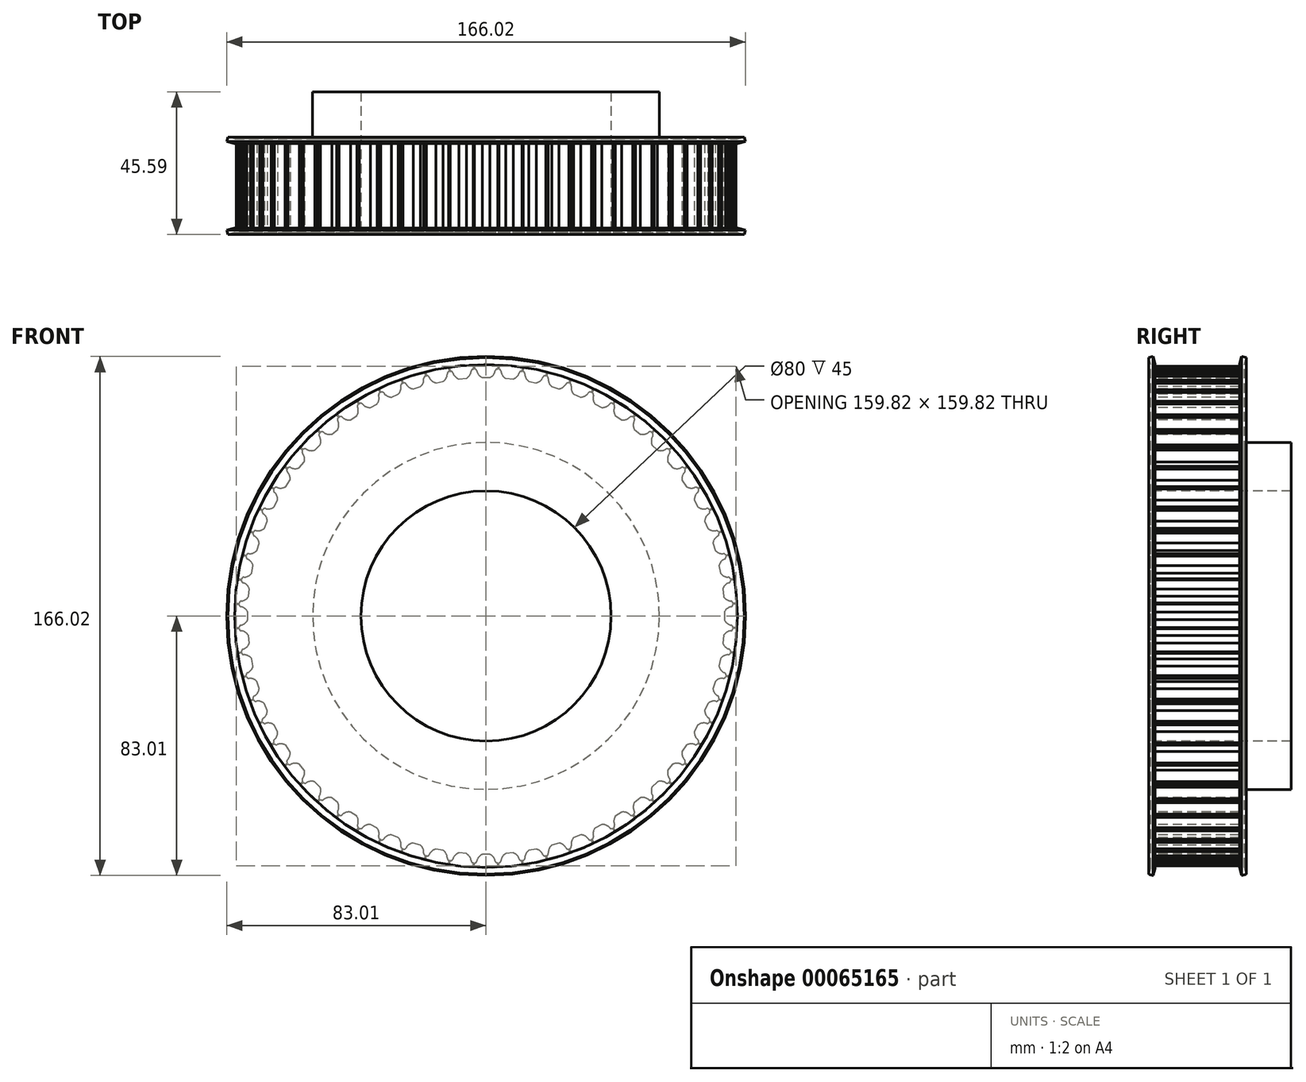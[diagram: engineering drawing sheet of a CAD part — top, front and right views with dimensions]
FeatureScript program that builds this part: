
annotation { "Feature Type Name" : "Feature", "Feature Type Description" : "" }
export const myFeature = defineFeature(function(context is Context, id is Id, definition is map)
    precondition{}
    {
        {
            var Q0;
            Q0=qCreatedBy(makeId("Right.planeOp"),FACE);
            var sketch = newSketch(context, id + "F0", { "sketchPlane" : qUnion([Q0])});
            skLineSegment(sketch, "E0", {"start": v(-21.52, 0) * mm, "end": v(23.89, 0) * mm, "construction": true});
            skLineSegment(sketch, "E1", {"start": v(0, 40) * mm, "end": v(0, 80) * mm});
            skLineSegment(sketch, "E2", {"start": v(0, 80) * mm, "end": v(30, 80) * mm});
            skLineSegment(sketch, "E3", {"start": v(30, 80) * mm, "end": v(30, 55.5) * mm});
            skLineSegment(sketch, "E4", {"start": v(30, 55.5) * mm, "end": v(45, 55.5) * mm});
            skLineSegment(sketch, "E5", {"start": v(45, 55.5) * mm, "end": v(45, 40) * mm});
            skLineSegment(sketch, "E6", {"start": v(45, 40) * mm, "end": v(0, 40) * mm});
            skSolve(sketch);
        }
        {
            var Q0;
            Q0=qSketchRegion(id+"F0",true);
            var Q1;
            Q1=sQuery(id+"F0.wireOp",EDGE,"E0");
            revolve(context, id + "F1", {"entities" : qUnion([Q0]), "axis" : qUnion([Q1]), "revolveType" : RevolveType.FULL});
        }
        {
            var Q0;
            Q0=qCreatedBy(makeId("Right.planeOp"),FACE);
            var sketch = newSketch(context, id + "F2", { "sketchPlane" : qUnion([Q0])});
            skLineSegment(sketch, "E7", {"start": v(-38.96, 0) * mm, "end": v(60.95, 0) * mm, "construction": true});
            skSolve(sketch);
        }
        {
            var Q0;
            Q0=makeQuery(id+"F1.opRevolve","SWEPT_FACE",FACE,{"disambiguationData":[OSD([sQuery(id+"F0.wireOp",EDGE,"E1")])]});
            var sketch = newSketch(context, id + "F3", { "sketchPlane" : qUnion([Q0])});
            skLineSegment(sketch, "E8.bottom", {"start": v(-3.75, 81) * mm, "end": v(3.75, 81) * mm});
            skLineSegment(sketch, "E8.top", {"start": v(3.67, 79) * mm, "end": v(3.75, 79) * mm});
            skLineSegment(sketch, "E8.left", {"start": v(-3.75, 81) * mm, "end": v(-3.75, 79) * mm});
            skLineSegment(sketch, "E8.right", {"start": v(3.75, 81) * mm, "end": v(3.75, 79) * mm});
            skArc(sketch, "E9", {"start": v(-2.94, 78.4) * mm, "mid": v(-2.33, 77.11) * mm, "end": v(-1.2, 76.25) * mm});
            skLineSegment(sketch, "E10", {"start": v(-1.2, 76.25) * mm, "end": v(1.2, 76.25) * mm});
            skArc(sketch, "E11.trimOffspring", {"start": v(1.2, 76.25) * mm, "mid": v(2.33, 77.11) * mm, "end": v(2.94, 78.4) * mm});
            skArc(sketch, "E12.filletArc", {"start": v(3.67, 79) * mm, "mid": v(3.2, 78.83) * mm, "end": v(2.94, 78.4) * mm});
            skLineSegment(sketch, "E13", {"start": v(-3.75, 79) * mm, "end": v(-3.67, 79) * mm});
            skPoint(sketch, "E14.visualSharp", {"position": v(-3, 79) * mm});
            skArc(sketch, "E14.filletArc", {"start": v(-2.94, 78.4) * mm, "mid": v(-3.2, 78.83) * mm, "end": v(-3.67, 79) * mm});
            skLineSegment(sketch, "E15.1.0", {"start": v(-11.67, 80.24) * mm, "end": v(-4.2, 80.98) * mm});
            skLineSegment(sketch, "E15.1.1", {"start": v(-11.67, 80.24) * mm, "end": v(-11.48, 78.25) * mm});
            skLineSegment(sketch, "E15.1.2", {"start": v(-11.48, 78.25) * mm, "end": v(-11.4, 78.26) * mm});
            skArc(sketch, "E15.1.3", {"start": v(-10.6, 77.73) * mm, "mid": v(-10.91, 78.14) * mm, "end": v(-11.4, 78.26) * mm});
            skArc(sketch, "E15.1.4", {"start": v(-10.6, 77.73) * mm, "mid": v(-9.88, 76.51) * mm, "end": v(-8.67, 75.77) * mm});
            skLineSegment(sketch, "E15.1.5", {"start": v(-8.67, 75.77) * mm, "end": v(-6.28, 76) * mm});
            skArc(sketch, "E15.1.6", {"start": v(-6.28, 76) * mm, "mid": v(-5.24, 76.97) * mm, "end": v(-4.76, 78.31) * mm});
            skArc(sketch, "E15.1.7", {"start": v(-4.09, 78.98) * mm, "mid": v(-4.54, 78.76) * mm, "end": v(-4.76, 78.31) * mm});
            skLineSegment(sketch, "E15.1.8", {"start": v(-4.09, 78.98) * mm, "end": v(-4.01, 78.99) * mm});
            skLineSegment(sketch, "E15.1.9", {"start": v(-4.2, 80.98) * mm, "end": v(-4.01, 78.99) * mm});
            skLineSegment(sketch, "E15.2.0", {"start": v(-19.48, 78.71) * mm, "end": v(-12.12, 80.18) * mm});
            skLineSegment(sketch, "E15.2.1", {"start": v(-19.48, 78.71) * mm, "end": v(-19.1, 76.75) * mm});
            skLineSegment(sketch, "E15.2.2", {"start": v(-19.1, 76.75) * mm, "end": v(-19.02, 76.77) * mm});
            skArc(sketch, "E15.2.3", {"start": v(-18.18, 76.32) * mm, "mid": v(-18.52, 76.7) * mm, "end": v(-19.02, 76.77) * mm});
            skArc(sketch, "E15.2.4", {"start": v(-18.18, 76.32) * mm, "mid": v(-17.33, 75.18) * mm, "end": v(-16.05, 74.55) * mm});
            skLineSegment(sketch, "E15.2.5", {"start": v(-16.05, 74.55) * mm, "end": v(-13.7, 75.02) * mm});
            skArc(sketch, "E15.2.6", {"start": v(-13.7, 75.02) * mm, "mid": v(-12.76, 76.09) * mm, "end": v(-12.41, 77.47) * mm});
            skArc(sketch, "E15.2.7", {"start": v(-11.8, 78.2) * mm, "mid": v(-12.24, 77.94) * mm, "end": v(-12.41, 77.47) * mm});
            skLineSegment(sketch, "E15.2.8", {"start": v(-11.8, 78.2) * mm, "end": v(-11.73, 78.21) * mm});
            skLineSegment(sketch, "E15.2.9", {"start": v(-12.12, 80.18) * mm, "end": v(-11.73, 78.21) * mm});
            skLineSegment(sketch, "E15.3.0", {"start": v(-27.1, 76.42) * mm, "end": v(-19.92, 78.6) * mm});
            skLineSegment(sketch, "E15.3.1", {"start": v(-27.1, 76.42) * mm, "end": v(-26.52, 74.5) * mm});
            skLineSegment(sketch, "E15.3.2", {"start": v(-26.52, 74.5) * mm, "end": v(-26.45, 74.53) * mm});
            skArc(sketch, "E15.3.3", {"start": v(-25.57, 74.17) * mm, "mid": v(-25.95, 74.5) * mm, "end": v(-26.45, 74.53) * mm});
            skArc(sketch, "E15.3.4", {"start": v(-25.57, 74.17) * mm, "mid": v(-24.62, 73.12) * mm, "end": v(-23.28, 72.62) * mm});
            skLineSegment(sketch, "E15.3.5", {"start": v(-23.28, 72.62) * mm, "end": v(-20.99, 73.31) * mm});
            skArc(sketch, "E15.3.6", {"start": v(-20.99, 73.31) * mm, "mid": v(-20.15, 74.47) * mm, "end": v(-19.95, 75.88) * mm});
            skArc(sketch, "E15.3.7", {"start": v(-19.42, 76.66) * mm, "mid": v(-19.82, 76.37) * mm, "end": v(-19.95, 75.88) * mm});
            skLineSegment(sketch, "E15.3.8", {"start": v(-19.42, 76.66) * mm, "end": v(-19.34, 76.69) * mm});
            skLineSegment(sketch, "E15.3.9", {"start": v(-19.92, 78.6) * mm, "end": v(-19.34, 76.69) * mm});
            skLineSegment(sketch, "E15.4.0", {"start": v(-34.46, 73.4) * mm, "end": v(-27.53, 76.27) * mm});
            skLineSegment(sketch, "E15.4.1", {"start": v(-34.46, 73.4) * mm, "end": v(-33.7, 71.55) * mm});
            skLineSegment(sketch, "E15.4.2", {"start": v(-33.7, 71.55) * mm, "end": v(-33.63, 71.58) * mm});
            skArc(sketch, "E15.4.3", {"start": v(-32.72, 71.3) * mm, "mid": v(-33.12, 71.6) * mm, "end": v(-33.63, 71.58) * mm});
            skArc(sketch, "E15.4.4", {"start": v(-32.72, 71.3) * mm, "mid": v(-31.66, 70.35) * mm, "end": v(-30.29, 69.99) * mm});
            skLineSegment(sketch, "E15.4.5", {"start": v(-30.29, 69.99) * mm, "end": v(-28.07, 70.9) * mm});
            skArc(sketch, "E15.4.6", {"start": v(-28.07, 70.9) * mm, "mid": v(-27.36, 72.13) * mm, "end": v(-27.29, 73.56) * mm});
            skArc(sketch, "E15.4.7", {"start": v(-26.84, 74.4) * mm, "mid": v(-27.21, 74.05) * mm, "end": v(-27.29, 73.56) * mm});
            skLineSegment(sketch, "E15.4.8", {"start": v(-26.84, 74.4) * mm, "end": v(-26.77, 74.42) * mm});
            skLineSegment(sketch, "E15.4.9", {"start": v(-27.53, 76.27) * mm, "end": v(-26.77, 74.42) * mm});
            skLineSegment(sketch, "E15.5.0", {"start": v(-41.5, 69.67) * mm, "end": v(-34.88, 73.2) * mm});
            skLineSegment(sketch, "E15.5.1", {"start": v(-41.5, 69.67) * mm, "end": v(-40.55, 67.9) * mm});
            skLineSegment(sketch, "E15.5.2", {"start": v(-40.55, 67.9) * mm, "end": v(-40.48, 67.94) * mm});
            skArc(sketch, "E15.5.3", {"start": v(-39.55, 67.76) * mm, "mid": v(-39.98, 68.01) * mm, "end": v(-40.48, 67.94) * mm});
            skArc(sketch, "E15.5.4", {"start": v(-39.55, 67.76) * mm, "mid": v(-38.4, 66.9) * mm, "end": v(-37, 66.68) * mm});
            skLineSegment(sketch, "E15.5.5", {"start": v(-37, 66.68) * mm, "end": v(-34.89, 67.81) * mm});
            skArc(sketch, "E15.5.6", {"start": v(-34.89, 67.81) * mm, "mid": v(-34.3, 69.1) * mm, "end": v(-34.37, 70.53) * mm});
            skArc(sketch, "E15.5.7", {"start": v(-34, 71.4) * mm, "mid": v(-34.34, 71.03) * mm, "end": v(-34.37, 70.53) * mm});
            skLineSegment(sketch, "E15.5.8", {"start": v(-34, 71.4) * mm, "end": v(-33.93, 71.44) * mm});
            skLineSegment(sketch, "E15.5.9", {"start": v(-34.88, 73.2) * mm, "end": v(-33.93, 71.44) * mm});
            skLineSegment(sketch, "E15.6.0", {"start": v(-48.12, 65.27) * mm, "end": v(-41.88, 69.43) * mm});
            skLineSegment(sketch, "E15.6.1", {"start": v(-48.12, 65.27) * mm, "end": v(-47, 63.6) * mm});
            skLineSegment(sketch, "E15.6.2", {"start": v(-47, 63.6) * mm, "end": v(-46.95, 63.64) * mm});
            skArc(sketch, "E15.6.3", {"start": v(-46, 63.55) * mm, "mid": v(-46.46, 63.77) * mm, "end": v(-46.95, 63.64) * mm});
            skArc(sketch, "E15.6.4", {"start": v(-46, 63.55) * mm, "mid": v(-44.78, 62.82) * mm, "end": v(-43.36, 62.73) * mm});
            skLineSegment(sketch, "E15.6.5", {"start": v(-43.36, 62.73) * mm, "end": v(-41.37, 64.07) * mm});
            skArc(sketch, "E15.6.6", {"start": v(-41.37, 64.07) * mm, "mid": v(-40.9, 65.41) * mm, "end": v(-41.11, 66.82) * mm});
            skArc(sketch, "E15.6.7", {"start": v(-40.84, 67.73) * mm, "mid": v(-41.14, 67.32) * mm, "end": v(-41.11, 66.82) * mm});
            skLineSegment(sketch, "E15.6.8", {"start": v(-40.84, 67.73) * mm, "end": v(-40.77, 67.77) * mm});
            skLineSegment(sketch, "E15.6.9", {"start": v(-41.88, 69.43) * mm, "end": v(-40.77, 67.77) * mm});
            skLineSegment(sketch, "E15.7.0", {"start": v(-54.28, 60.23) * mm, "end": v(-48.49, 65) * mm});
            skLineSegment(sketch, "E15.7.1", {"start": v(-54.28, 60.23) * mm, "end": v(-53.02, 58.69) * mm});
            skLineSegment(sketch, "E15.7.2", {"start": v(-53.02, 58.69) * mm, "end": v(-52.96, 58.74) * mm});
            skArc(sketch, "E15.7.3", {"start": v(-52, 58.74) * mm, "mid": v(-52.48, 58.9) * mm, "end": v(-52.96, 58.74) * mm});
            skArc(sketch, "E15.7.4", {"start": v(-52, 58.74) * mm, "mid": v(-50.72, 58.13) * mm, "end": v(-49.3, 58.18) * mm});
            skLineSegment(sketch, "E15.7.5", {"start": v(-49.3, 58.18) * mm, "end": v(-47.45, 59.7) * mm});
            skArc(sketch, "E15.7.6", {"start": v(-47.45, 59.7) * mm, "mid": v(-47.12, 61.09) * mm, "end": v(-47.46, 62.47) * mm});
            skArc(sketch, "E15.7.7", {"start": v(-47.28, 63.4) * mm, "mid": v(-47.54, 62.97) * mm, "end": v(-47.46, 62.47) * mm});
            skLineSegment(sketch, "E15.7.8", {"start": v(-47.28, 63.4) * mm, "end": v(-47.22, 63.45) * mm});
            skLineSegment(sketch, "E15.7.9", {"start": v(-48.49, 65) * mm, "end": v(-47.22, 63.45) * mm});
            skLineSegment(sketch, "E15.8.0", {"start": v(-59.93, 54.62) * mm, "end": v(-54.62, 59.93) * mm});
            skLineSegment(sketch, "E15.8.1", {"start": v(-59.93, 54.62) * mm, "end": v(-58.51, 53.2) * mm});
            skLineSegment(sketch, "E15.8.2", {"start": v(-58.51, 53.2) * mm, "end": v(-58.46, 53.26) * mm});
            skArc(sketch, "E15.8.3", {"start": v(-57.52, 53.36) * mm, "mid": v(-58, 53.48) * mm, "end": v(-58.46, 53.26) * mm});
            skArc(sketch, "E15.8.4", {"start": v(-57.52, 53.36) * mm, "mid": v(-56.18, 52.88) * mm, "end": v(-54.76, 53.07) * mm});
            skLineSegment(sketch, "E15.8.5", {"start": v(-54.76, 53.07) * mm, "end": v(-53.07, 54.76) * mm});
            skArc(sketch, "E15.8.6", {"start": v(-53.07, 54.76) * mm, "mid": v(-52.88, 56.18) * mm, "end": v(-53.36, 57.52) * mm});
            skArc(sketch, "E15.8.7", {"start": v(-53.26, 58.46) * mm, "mid": v(-53.48, 58) * mm, "end": v(-53.36, 57.52) * mm});
            skLineSegment(sketch, "E15.8.8", {"start": v(-53.26, 58.46) * mm, "end": v(-53.2, 58.51) * mm});
            skLineSegment(sketch, "E15.8.9", {"start": v(-54.62, 59.93) * mm, "end": v(-53.2, 58.51) * mm});
            skLineSegment(sketch, "E15.9.0", {"start": v(-65, 48.49) * mm, "end": v(-60.23, 54.28) * mm});
            skLineSegment(sketch, "E15.9.1", {"start": v(-65, 48.49) * mm, "end": v(-63.45, 47.22) * mm});
            skLineSegment(sketch, "E15.9.2", {"start": v(-63.45, 47.22) * mm, "end": v(-63.4, 47.28) * mm});
            skArc(sketch, "E15.9.3", {"start": v(-62.47, 47.46) * mm, "mid": v(-62.97, 47.54) * mm, "end": v(-63.4, 47.28) * mm});
            skArc(sketch, "E15.9.4", {"start": v(-62.47, 47.46) * mm, "mid": v(-61.09, 47.12) * mm, "end": v(-59.7, 47.45) * mm});
            skLineSegment(sketch, "E15.9.5", {"start": v(-59.7, 47.45) * mm, "end": v(-58.18, 49.3) * mm});
            skArc(sketch, "E15.9.6", {"start": v(-58.18, 49.3) * mm, "mid": v(-58.13, 50.72) * mm, "end": v(-58.74, 52) * mm});
            skArc(sketch, "E15.9.7", {"start": v(-58.74, 52.96) * mm, "mid": v(-58.9, 52.48) * mm, "end": v(-58.74, 52) * mm});
            skLineSegment(sketch, "E15.9.8", {"start": v(-58.74, 52.96) * mm, "end": v(-58.69, 53.02) * mm});
            skLineSegment(sketch, "E15.9.9", {"start": v(-60.23, 54.28) * mm, "end": v(-58.69, 53.02) * mm});
            skLineSegment(sketch, "E15.10.0", {"start": v(-69.43, 41.88) * mm, "end": v(-65.27, 48.12) * mm});
            skLineSegment(sketch, "E15.10.1", {"start": v(-69.43, 41.88) * mm, "end": v(-67.77, 40.77) * mm});
            skLineSegment(sketch, "E15.10.2", {"start": v(-67.77, 40.77) * mm, "end": v(-67.73, 40.84) * mm});
            skArc(sketch, "E15.10.3", {"start": v(-66.82, 41.11) * mm, "mid": v(-67.32, 41.14) * mm, "end": v(-67.73, 40.84) * mm});
            skArc(sketch, "E15.10.4", {"start": v(-66.82, 41.11) * mm, "mid": v(-65.41, 40.9) * mm, "end": v(-64.07, 41.37) * mm});
            skLineSegment(sketch, "E15.10.5", {"start": v(-64.07, 41.37) * mm, "end": v(-62.73, 43.36) * mm});
            skArc(sketch, "E15.10.6", {"start": v(-62.73, 43.36) * mm, "mid": v(-62.82, 44.78) * mm, "end": v(-63.55, 46) * mm});
            skArc(sketch, "E15.10.7", {"start": v(-63.64, 46.95) * mm, "mid": v(-63.77, 46.46) * mm, "end": v(-63.55, 46) * mm});
            skLineSegment(sketch, "E15.10.8", {"start": v(-63.64, 46.95) * mm, "end": v(-63.6, 47) * mm});
            skLineSegment(sketch, "E15.10.9", {"start": v(-65.27, 48.12) * mm, "end": v(-63.6, 47) * mm});
            skLineSegment(sketch, "E15.11.0", {"start": v(-73.2, 34.88) * mm, "end": v(-69.67, 41.5) * mm});
            skLineSegment(sketch, "E15.11.1", {"start": v(-73.2, 34.88) * mm, "end": v(-71.44, 33.93) * mm});
            skLineSegment(sketch, "E15.11.2", {"start": v(-71.44, 33.93) * mm, "end": v(-71.4, 34) * mm});
            skArc(sketch, "E15.11.3", {"start": v(-70.53, 34.37) * mm, "mid": v(-71.03, 34.34) * mm, "end": v(-71.4, 34) * mm});
            skArc(sketch, "E15.11.4", {"start": v(-70.53, 34.37) * mm, "mid": v(-69.1, 34.3) * mm, "end": v(-67.81, 34.89) * mm});
            skLineSegment(sketch, "E15.11.5", {"start": v(-67.81, 34.89) * mm, "end": v(-66.68, 37) * mm});
            skArc(sketch, "E15.11.6", {"start": v(-66.68, 37) * mm, "mid": v(-66.9, 38.4) * mm, "end": v(-67.76, 39.55) * mm});
            skArc(sketch, "E15.11.7", {"start": v(-67.94, 40.48) * mm, "mid": v(-68.01, 39.98) * mm, "end": v(-67.76, 39.55) * mm});
            skLineSegment(sketch, "E15.11.8", {"start": v(-67.94, 40.48) * mm, "end": v(-67.9, 40.55) * mm});
            skLineSegment(sketch, "E15.11.9", {"start": v(-69.67, 41.5) * mm, "end": v(-67.9, 40.55) * mm});
            skLineSegment(sketch, "E15.12.0", {"start": v(-76.27, 27.53) * mm, "end": v(-73.4, 34.46) * mm});
            skLineSegment(sketch, "E15.12.1", {"start": v(-76.27, 27.53) * mm, "end": v(-74.42, 26.77) * mm});
            skLineSegment(sketch, "E15.12.2", {"start": v(-74.42, 26.77) * mm, "end": v(-74.4, 26.84) * mm});
            skArc(sketch, "E15.12.3", {"start": v(-73.56, 27.29) * mm, "mid": v(-74.05, 27.21) * mm, "end": v(-74.4, 26.84) * mm});
            skArc(sketch, "E15.12.4", {"start": v(-73.56, 27.29) * mm, "mid": v(-72.13, 27.36) * mm, "end": v(-70.9, 28.07) * mm});
            skLineSegment(sketch, "E15.12.5", {"start": v(-70.9, 28.07) * mm, "end": v(-69.99, 30.29) * mm});
            skArc(sketch, "E15.12.6", {"start": v(-69.99, 30.29) * mm, "mid": v(-70.35, 31.66) * mm, "end": v(-71.3, 32.72) * mm});
            skArc(sketch, "E15.12.7", {"start": v(-71.58, 33.63) * mm, "mid": v(-71.6, 33.12) * mm, "end": v(-71.3, 32.72) * mm});
            skLineSegment(sketch, "E15.12.8", {"start": v(-71.58, 33.63) * mm, "end": v(-71.55, 33.7) * mm});
            skLineSegment(sketch, "E15.12.9", {"start": v(-73.4, 34.46) * mm, "end": v(-71.55, 33.7) * mm});
            skLineSegment(sketch, "E15.13.0", {"start": v(-78.6, 19.92) * mm, "end": v(-76.42, 27.1) * mm});
            skLineSegment(sketch, "E15.13.1", {"start": v(-78.6, 19.92) * mm, "end": v(-76.69, 19.34) * mm});
            skLineSegment(sketch, "E15.13.2", {"start": v(-76.69, 19.34) * mm, "end": v(-76.66, 19.42) * mm});
            skArc(sketch, "E15.13.3", {"start": v(-75.88, 19.95) * mm, "mid": v(-76.37, 19.82) * mm, "end": v(-76.66, 19.42) * mm});
            skArc(sketch, "E15.13.4", {"start": v(-75.88, 19.95) * mm, "mid": v(-74.47, 20.15) * mm, "end": v(-73.31, 20.99) * mm});
            skLineSegment(sketch, "E15.13.5", {"start": v(-73.31, 20.99) * mm, "end": v(-72.62, 23.28) * mm});
            skArc(sketch, "E15.13.6", {"start": v(-72.62, 23.28) * mm, "mid": v(-73.12, 24.62) * mm, "end": v(-74.17, 25.57) * mm});
            skArc(sketch, "E15.13.7", {"start": v(-74.53, 26.45) * mm, "mid": v(-74.5, 25.95) * mm, "end": v(-74.17, 25.57) * mm});
            skLineSegment(sketch, "E15.13.8", {"start": v(-74.53, 26.45) * mm, "end": v(-74.5, 26.52) * mm});
            skLineSegment(sketch, "E15.13.9", {"start": v(-76.42, 27.1) * mm, "end": v(-74.5, 26.52) * mm});
            skLineSegment(sketch, "E15.14.0", {"start": v(-80.18, 12.12) * mm, "end": v(-78.71, 19.48) * mm});
            skLineSegment(sketch, "E15.14.1", {"start": v(-80.18, 12.12) * mm, "end": v(-78.21, 11.73) * mm});
            skLineSegment(sketch, "E15.14.2", {"start": v(-78.21, 11.73) * mm, "end": v(-78.2, 11.8) * mm});
            skArc(sketch, "E15.14.3", {"start": v(-77.47, 12.41) * mm, "mid": v(-77.94, 12.24) * mm, "end": v(-78.2, 11.8) * mm});
            skArc(sketch, "E15.14.4", {"start": v(-77.47, 12.41) * mm, "mid": v(-76.09, 12.76) * mm, "end": v(-75.02, 13.7) * mm});
            skLineSegment(sketch, "E15.14.5", {"start": v(-75.02, 13.7) * mm, "end": v(-74.55, 16.05) * mm});
            skArc(sketch, "E15.14.6", {"start": v(-74.55, 16.05) * mm, "mid": v(-75.18, 17.33) * mm, "end": v(-76.32, 18.18) * mm});
            skArc(sketch, "E15.14.7", {"start": v(-76.77, 19.02) * mm, "mid": v(-76.7, 18.52) * mm, "end": v(-76.32, 18.18) * mm});
            skLineSegment(sketch, "E15.14.8", {"start": v(-76.77, 19.02) * mm, "end": v(-76.75, 19.1) * mm});
            skLineSegment(sketch, "E15.14.9", {"start": v(-78.71, 19.48) * mm, "end": v(-76.75, 19.1) * mm});
            skLineSegment(sketch, "E15.15.0", {"start": v(-80.98, 4.2) * mm, "end": v(-80.24, 11.67) * mm});
            skLineSegment(sketch, "E15.15.1", {"start": v(-80.98, 4.2) * mm, "end": v(-78.99, 4.01) * mm});
            skLineSegment(sketch, "E15.15.2", {"start": v(-78.99, 4.01) * mm, "end": v(-78.98, 4.09) * mm});
            skArc(sketch, "E15.15.3", {"start": v(-78.31, 4.76) * mm, "mid": v(-78.76, 4.54) * mm, "end": v(-78.98, 4.09) * mm});
            skArc(sketch, "E15.15.4", {"start": v(-78.31, 4.76) * mm, "mid": v(-76.97, 5.24) * mm, "end": v(-76, 6.28) * mm});
            skLineSegment(sketch, "E15.15.5", {"start": v(-76, 6.28) * mm, "end": v(-75.77, 8.67) * mm});
            skArc(sketch, "E15.15.6", {"start": v(-75.77, 8.67) * mm, "mid": v(-76.51, 9.88) * mm, "end": v(-77.73, 10.6) * mm});
            skArc(sketch, "E15.15.7", {"start": v(-78.26, 11.4) * mm, "mid": v(-78.14, 10.91) * mm, "end": v(-77.73, 10.6) * mm});
            skLineSegment(sketch, "E15.15.8", {"start": v(-78.26, 11.4) * mm, "end": v(-78.25, 11.48) * mm});
            skLineSegment(sketch, "E15.15.9", {"start": v(-80.24, 11.67) * mm, "end": v(-78.25, 11.48) * mm});
            skLineSegment(sketch, "E15.16.0", {"start": v(-81, -3.75) * mm, "end": v(-81, 3.75) * mm});
            skLineSegment(sketch, "E15.16.1", {"start": v(-81, -3.75) * mm, "end": v(-79, -3.75) * mm});
            skLineSegment(sketch, "E15.16.2", {"start": v(-79, -3.75) * mm, "end": v(-79, -3.67) * mm});
            skArc(sketch, "E15.16.3", {"start": v(-78.4, -2.94) * mm, "mid": v(-78.83, -3.2) * mm, "end": v(-79, -3.67) * mm});
            skArc(sketch, "E15.16.4", {"start": v(-78.4, -2.94) * mm, "mid": v(-77.11, -2.33) * mm, "end": v(-76.25, -1.2) * mm});
            skLineSegment(sketch, "E15.16.5", {"start": v(-76.25, -1.2) * mm, "end": v(-76.25, 1.2) * mm});
            skArc(sketch, "E15.16.6", {"start": v(-76.25, 1.2) * mm, "mid": v(-77.11, 2.33) * mm, "end": v(-78.4, 2.94) * mm});
            skArc(sketch, "E15.16.7", {"start": v(-79, 3.67) * mm, "mid": v(-78.83, 3.2) * mm, "end": v(-78.4, 2.94) * mm});
            skLineSegment(sketch, "E15.16.8", {"start": v(-79, 3.67) * mm, "end": v(-79, 3.75) * mm});
            skLineSegment(sketch, "E15.16.9", {"start": v(-81, 3.75) * mm, "end": v(-79, 3.75) * mm});
            skLineSegment(sketch, "E15.17.0", {"start": v(-80.24, -11.67) * mm, "end": v(-80.98, -4.2) * mm});
            skLineSegment(sketch, "E15.17.1", {"start": v(-80.24, -11.67) * mm, "end": v(-78.25, -11.48) * mm});
            skLineSegment(sketch, "E15.17.2", {"start": v(-78.25, -11.48) * mm, "end": v(-78.26, -11.4) * mm});
            skArc(sketch, "E15.17.3", {"start": v(-77.73, -10.6) * mm, "mid": v(-78.14, -10.91) * mm, "end": v(-78.26, -11.4) * mm});
            skArc(sketch, "E15.17.4", {"start": v(-77.73, -10.6) * mm, "mid": v(-76.51, -9.88) * mm, "end": v(-75.77, -8.67) * mm});
            skLineSegment(sketch, "E15.17.5", {"start": v(-75.77, -8.67) * mm, "end": v(-76, -6.28) * mm});
            skArc(sketch, "E15.17.6", {"start": v(-76, -6.28) * mm, "mid": v(-76.97, -5.24) * mm, "end": v(-78.31, -4.76) * mm});
            skArc(sketch, "E15.17.7", {"start": v(-78.98, -4.09) * mm, "mid": v(-78.76, -4.54) * mm, "end": v(-78.31, -4.76) * mm});
            skLineSegment(sketch, "E15.17.8", {"start": v(-78.98, -4.09) * mm, "end": v(-78.99, -4.01) * mm});
            skLineSegment(sketch, "E15.17.9", {"start": v(-80.98, -4.2) * mm, "end": v(-78.99, -4.01) * mm});
            skLineSegment(sketch, "E15.18.0", {"start": v(-78.71, -19.48) * mm, "end": v(-80.18, -12.12) * mm});
            skLineSegment(sketch, "E15.18.1", {"start": v(-78.71, -19.48) * mm, "end": v(-76.75, -19.1) * mm});
            skLineSegment(sketch, "E15.18.2", {"start": v(-76.75, -19.1) * mm, "end": v(-76.77, -19.02) * mm});
            skArc(sketch, "E15.18.3", {"start": v(-76.32, -18.18) * mm, "mid": v(-76.7, -18.52) * mm, "end": v(-76.77, -19.02) * mm});
            skArc(sketch, "E15.18.4", {"start": v(-76.32, -18.18) * mm, "mid": v(-75.18, -17.33) * mm, "end": v(-74.55, -16.05) * mm});
            skLineSegment(sketch, "E15.18.5", {"start": v(-74.55, -16.05) * mm, "end": v(-75.02, -13.7) * mm});
            skArc(sketch, "E15.18.6", {"start": v(-75.02, -13.7) * mm, "mid": v(-76.09, -12.76) * mm, "end": v(-77.47, -12.41) * mm});
            skArc(sketch, "E15.18.7", {"start": v(-78.2, -11.8) * mm, "mid": v(-77.94, -12.24) * mm, "end": v(-77.47, -12.41) * mm});
            skLineSegment(sketch, "E15.18.8", {"start": v(-78.2, -11.8) * mm, "end": v(-78.21, -11.73) * mm});
            skLineSegment(sketch, "E15.18.9", {"start": v(-80.18, -12.12) * mm, "end": v(-78.21, -11.73) * mm});
            skLineSegment(sketch, "E15.19.0", {"start": v(-76.42, -27.1) * mm, "end": v(-78.6, -19.92) * mm});
            skLineSegment(sketch, "E15.19.1", {"start": v(-76.42, -27.1) * mm, "end": v(-74.5, -26.52) * mm});
            skLineSegment(sketch, "E15.19.2", {"start": v(-74.5, -26.52) * mm, "end": v(-74.53, -26.45) * mm});
            skArc(sketch, "E15.19.3", {"start": v(-74.17, -25.57) * mm, "mid": v(-74.5, -25.95) * mm, "end": v(-74.53, -26.45) * mm});
            skArc(sketch, "E15.19.4", {"start": v(-74.17, -25.57) * mm, "mid": v(-73.12, -24.62) * mm, "end": v(-72.62, -23.28) * mm});
            skLineSegment(sketch, "E15.19.5", {"start": v(-72.62, -23.28) * mm, "end": v(-73.31, -20.99) * mm});
            skArc(sketch, "E15.19.6", {"start": v(-73.31, -20.99) * mm, "mid": v(-74.47, -20.15) * mm, "end": v(-75.88, -19.95) * mm});
            skArc(sketch, "E15.19.7", {"start": v(-76.66, -19.42) * mm, "mid": v(-76.37, -19.82) * mm, "end": v(-75.88, -19.95) * mm});
            skLineSegment(sketch, "E15.19.8", {"start": v(-76.66, -19.42) * mm, "end": v(-76.69, -19.34) * mm});
            skLineSegment(sketch, "E15.19.9", {"start": v(-78.6, -19.92) * mm, "end": v(-76.69, -19.34) * mm});
            skLineSegment(sketch, "E15.20.0", {"start": v(-73.4, -34.46) * mm, "end": v(-76.27, -27.53) * mm});
            skLineSegment(sketch, "E15.20.1", {"start": v(-73.4, -34.46) * mm, "end": v(-71.55, -33.7) * mm});
            skLineSegment(sketch, "E15.20.2", {"start": v(-71.55, -33.7) * mm, "end": v(-71.58, -33.63) * mm});
            skArc(sketch, "E15.20.3", {"start": v(-71.3, -32.72) * mm, "mid": v(-71.6, -33.12) * mm, "end": v(-71.58, -33.63) * mm});
            skArc(sketch, "E15.20.4", {"start": v(-71.3, -32.72) * mm, "mid": v(-70.35, -31.66) * mm, "end": v(-69.99, -30.29) * mm});
            skLineSegment(sketch, "E15.20.5", {"start": v(-69.99, -30.29) * mm, "end": v(-70.9, -28.07) * mm});
            skArc(sketch, "E15.20.6", {"start": v(-70.9, -28.07) * mm, "mid": v(-72.13, -27.36) * mm, "end": v(-73.56, -27.29) * mm});
            skArc(sketch, "E15.20.7", {"start": v(-74.4, -26.84) * mm, "mid": v(-74.05, -27.21) * mm, "end": v(-73.56, -27.29) * mm});
            skLineSegment(sketch, "E15.20.8", {"start": v(-74.4, -26.84) * mm, "end": v(-74.42, -26.77) * mm});
            skLineSegment(sketch, "E15.20.9", {"start": v(-76.27, -27.53) * mm, "end": v(-74.42, -26.77) * mm});
            skLineSegment(sketch, "E15.21.0", {"start": v(-69.67, -41.5) * mm, "end": v(-73.2, -34.88) * mm});
            skLineSegment(sketch, "E15.21.1", {"start": v(-69.67, -41.5) * mm, "end": v(-67.9, -40.55) * mm});
            skLineSegment(sketch, "E15.21.2", {"start": v(-67.9, -40.55) * mm, "end": v(-67.94, -40.48) * mm});
            skArc(sketch, "E15.21.3", {"start": v(-67.76, -39.55) * mm, "mid": v(-68.01, -39.98) * mm, "end": v(-67.94, -40.48) * mm});
            skArc(sketch, "E15.21.4", {"start": v(-67.76, -39.55) * mm, "mid": v(-66.9, -38.4) * mm, "end": v(-66.68, -37) * mm});
            skLineSegment(sketch, "E15.21.5", {"start": v(-66.68, -37) * mm, "end": v(-67.81, -34.89) * mm});
            skArc(sketch, "E15.21.6", {"start": v(-67.81, -34.89) * mm, "mid": v(-69.1, -34.3) * mm, "end": v(-70.53, -34.37) * mm});
            skArc(sketch, "E15.21.7", {"start": v(-71.4, -34) * mm, "mid": v(-71.03, -34.34) * mm, "end": v(-70.53, -34.37) * mm});
            skLineSegment(sketch, "E15.21.8", {"start": v(-71.4, -34) * mm, "end": v(-71.44, -33.93) * mm});
            skLineSegment(sketch, "E15.21.9", {"start": v(-73.2, -34.88) * mm, "end": v(-71.44, -33.93) * mm});
            skPoint(sketch, "E15.center", {"position": v(0, 0) * mm});
            skLineSegment(sketch, "E16.1.22.0", {"start": v(-65.27, -48.12) * mm, "end": v(-69.43, -41.88) * mm});
            skLineSegment(sketch, "E16.3.22.0", {"start": v(-65.27, -48.12) * mm, "end": v(-63.6, -47) * mm});
            skLineSegment(sketch, "E16.6.22.0", {"start": v(-63.6, -47) * mm, "end": v(-63.64, -46.95) * mm});
            skArc(sketch, "E16.9.22.0", {"start": v(-63.55, -46) * mm, "mid": v(-63.77, -46.46) * mm, "end": v(-63.64, -46.95) * mm});
            skArc(sketch, "E16.13.22.0", {"start": v(-63.55, -46) * mm, "mid": v(-62.82, -44.78) * mm, "end": v(-62.73, -43.36) * mm});
            skLineSegment(sketch, "E16.17.22.0", {"start": v(-62.73, -43.36) * mm, "end": v(-64.07, -41.37) * mm});
            skArc(sketch, "E16.20.22.0", {"start": v(-64.07, -41.37) * mm, "mid": v(-65.41, -40.9) * mm, "end": v(-66.82, -41.11) * mm});
            skArc(sketch, "E16.24.22.0", {"start": v(-67.73, -40.84) * mm, "mid": v(-67.32, -41.14) * mm, "end": v(-66.82, -41.11) * mm});
            skLineSegment(sketch, "E16.28.22.0", {"start": v(-67.73, -40.84) * mm, "end": v(-67.77, -40.77) * mm});
            skLineSegment(sketch, "E16.31.22.0", {"start": v(-69.43, -41.88) * mm, "end": v(-67.77, -40.77) * mm});
            skLineSegment(sketch, "E16.1.23.0", {"start": v(-60.23, -54.28) * mm, "end": v(-65, -48.49) * mm});
            skLineSegment(sketch, "E16.3.23.0", {"start": v(-60.23, -54.28) * mm, "end": v(-58.69, -53.02) * mm});
            skLineSegment(sketch, "E16.6.23.0", {"start": v(-58.69, -53.02) * mm, "end": v(-58.74, -52.96) * mm});
            skArc(sketch, "E16.9.23.0", {"start": v(-58.74, -52) * mm, "mid": v(-58.9, -52.48) * mm, "end": v(-58.74, -52.96) * mm});
            skArc(sketch, "E16.13.23.0", {"start": v(-58.74, -52) * mm, "mid": v(-58.13, -50.72) * mm, "end": v(-58.18, -49.3) * mm});
            skLineSegment(sketch, "E16.17.23.0", {"start": v(-58.18, -49.3) * mm, "end": v(-59.7, -47.45) * mm});
            skArc(sketch, "E16.20.23.0", {"start": v(-59.7, -47.45) * mm, "mid": v(-61.09, -47.12) * mm, "end": v(-62.47, -47.46) * mm});
            skArc(sketch, "E16.24.23.0", {"start": v(-63.4, -47.28) * mm, "mid": v(-62.97, -47.54) * mm, "end": v(-62.47, -47.46) * mm});
            skLineSegment(sketch, "E16.28.23.0", {"start": v(-63.4, -47.28) * mm, "end": v(-63.45, -47.22) * mm});
            skLineSegment(sketch, "E16.31.23.0", {"start": v(-65, -48.49) * mm, "end": v(-63.45, -47.22) * mm});
            skLineSegment(sketch, "E16.1.24.0", {"start": v(-54.62, -59.93) * mm, "end": v(-59.93, -54.62) * mm});
            skLineSegment(sketch, "E16.3.24.0", {"start": v(-54.62, -59.93) * mm, "end": v(-53.2, -58.51) * mm});
            skLineSegment(sketch, "E16.6.24.0", {"start": v(-53.2, -58.51) * mm, "end": v(-53.26, -58.46) * mm});
            skArc(sketch, "E16.9.24.0", {"start": v(-53.36, -57.52) * mm, "mid": v(-53.48, -58) * mm, "end": v(-53.26, -58.46) * mm});
            skArc(sketch, "E16.13.24.0", {"start": v(-53.36, -57.52) * mm, "mid": v(-52.88, -56.18) * mm, "end": v(-53.07, -54.76) * mm});
            skLineSegment(sketch, "E16.17.24.0", {"start": v(-53.07, -54.76) * mm, "end": v(-54.76, -53.07) * mm});
            skArc(sketch, "E16.20.24.0", {"start": v(-54.76, -53.07) * mm, "mid": v(-56.18, -52.88) * mm, "end": v(-57.52, -53.36) * mm});
            skArc(sketch, "E16.24.24.0", {"start": v(-58.46, -53.26) * mm, "mid": v(-58, -53.48) * mm, "end": v(-57.52, -53.36) * mm});
            skLineSegment(sketch, "E16.28.24.0", {"start": v(-58.46, -53.26) * mm, "end": v(-58.51, -53.2) * mm});
            skLineSegment(sketch, "E16.31.24.0", {"start": v(-59.93, -54.62) * mm, "end": v(-58.51, -53.2) * mm});
            skLineSegment(sketch, "E16.1.25.0", {"start": v(-48.49, -65) * mm, "end": v(-54.28, -60.23) * mm});
            skLineSegment(sketch, "E16.3.25.0", {"start": v(-48.49, -65) * mm, "end": v(-47.22, -63.45) * mm});
            skLineSegment(sketch, "E16.6.25.0", {"start": v(-47.22, -63.45) * mm, "end": v(-47.28, -63.4) * mm});
            skArc(sketch, "E16.9.25.0", {"start": v(-47.46, -62.47) * mm, "mid": v(-47.54, -62.97) * mm, "end": v(-47.28, -63.4) * mm});
            skArc(sketch, "E16.13.25.0", {"start": v(-47.46, -62.47) * mm, "mid": v(-47.12, -61.09) * mm, "end": v(-47.45, -59.7) * mm});
            skLineSegment(sketch, "E16.17.25.0", {"start": v(-47.45, -59.7) * mm, "end": v(-49.3, -58.18) * mm});
            skArc(sketch, "E16.20.25.0", {"start": v(-49.3, -58.18) * mm, "mid": v(-50.72, -58.13) * mm, "end": v(-52, -58.74) * mm});
            skArc(sketch, "E16.24.25.0", {"start": v(-52.96, -58.74) * mm, "mid": v(-52.48, -58.9) * mm, "end": v(-52, -58.74) * mm});
            skLineSegment(sketch, "E16.28.25.0", {"start": v(-52.96, -58.74) * mm, "end": v(-53.02, -58.69) * mm});
            skLineSegment(sketch, "E16.31.25.0", {"start": v(-54.28, -60.23) * mm, "end": v(-53.02, -58.69) * mm});
            skLineSegment(sketch, "E16.1.26.0", {"start": v(-41.88, -69.43) * mm, "end": v(-48.12, -65.27) * mm});
            skLineSegment(sketch, "E16.3.26.0", {"start": v(-41.88, -69.43) * mm, "end": v(-40.77, -67.77) * mm});
            skLineSegment(sketch, "E16.6.26.0", {"start": v(-40.77, -67.77) * mm, "end": v(-40.84, -67.73) * mm});
            skArc(sketch, "E16.9.26.0", {"start": v(-41.11, -66.82) * mm, "mid": v(-41.14, -67.32) * mm, "end": v(-40.84, -67.73) * mm});
            skArc(sketch, "E16.13.26.0", {"start": v(-41.11, -66.82) * mm, "mid": v(-40.9, -65.41) * mm, "end": v(-41.37, -64.07) * mm});
            skLineSegment(sketch, "E16.17.26.0", {"start": v(-41.37, -64.07) * mm, "end": v(-43.36, -62.73) * mm});
            skArc(sketch, "E16.20.26.0", {"start": v(-43.36, -62.73) * mm, "mid": v(-44.78, -62.82) * mm, "end": v(-46, -63.55) * mm});
            skArc(sketch, "E16.24.26.0", {"start": v(-46.95, -63.64) * mm, "mid": v(-46.46, -63.77) * mm, "end": v(-46, -63.55) * mm});
            skLineSegment(sketch, "E16.28.26.0", {"start": v(-46.95, -63.64) * mm, "end": v(-47, -63.6) * mm});
            skLineSegment(sketch, "E16.31.26.0", {"start": v(-48.12, -65.27) * mm, "end": v(-47, -63.6) * mm});
            skLineSegment(sketch, "E16.1.27.0", {"start": v(-34.88, -73.2) * mm, "end": v(-41.5, -69.67) * mm});
            skLineSegment(sketch, "E16.3.27.0", {"start": v(-34.88, -73.2) * mm, "end": v(-33.93, -71.44) * mm});
            skLineSegment(sketch, "E16.6.27.0", {"start": v(-33.93, -71.44) * mm, "end": v(-34, -71.4) * mm});
            skArc(sketch, "E16.9.27.0", {"start": v(-34.37, -70.53) * mm, "mid": v(-34.34, -71.03) * mm, "end": v(-34, -71.4) * mm});
            skArc(sketch, "E16.13.27.0", {"start": v(-34.37, -70.53) * mm, "mid": v(-34.3, -69.1) * mm, "end": v(-34.89, -67.81) * mm});
            skLineSegment(sketch, "E16.17.27.0", {"start": v(-34.89, -67.81) * mm, "end": v(-37, -66.68) * mm});
            skArc(sketch, "E16.20.27.0", {"start": v(-37, -66.68) * mm, "mid": v(-38.4, -66.9) * mm, "end": v(-39.55, -67.76) * mm});
            skArc(sketch, "E16.24.27.0", {"start": v(-40.48, -67.94) * mm, "mid": v(-39.98, -68.01) * mm, "end": v(-39.55, -67.76) * mm});
            skLineSegment(sketch, "E16.28.27.0", {"start": v(-40.48, -67.94) * mm, "end": v(-40.55, -67.9) * mm});
            skLineSegment(sketch, "E16.31.27.0", {"start": v(-41.5, -69.67) * mm, "end": v(-40.55, -67.9) * mm});
            skLineSegment(sketch, "E16.1.28.0", {"start": v(-27.53, -76.27) * mm, "end": v(-34.46, -73.4) * mm});
            skLineSegment(sketch, "E16.3.28.0", {"start": v(-27.53, -76.27) * mm, "end": v(-26.77, -74.42) * mm});
            skLineSegment(sketch, "E16.6.28.0", {"start": v(-26.77, -74.42) * mm, "end": v(-26.84, -74.4) * mm});
            skArc(sketch, "E16.9.28.0", {"start": v(-27.29, -73.56) * mm, "mid": v(-27.21, -74.05) * mm, "end": v(-26.84, -74.4) * mm});
            skArc(sketch, "E16.13.28.0", {"start": v(-27.29, -73.56) * mm, "mid": v(-27.36, -72.13) * mm, "end": v(-28.07, -70.9) * mm});
            skLineSegment(sketch, "E16.17.28.0", {"start": v(-28.07, -70.9) * mm, "end": v(-30.29, -69.99) * mm});
            skArc(sketch, "E16.20.28.0", {"start": v(-30.29, -69.99) * mm, "mid": v(-31.66, -70.35) * mm, "end": v(-32.72, -71.3) * mm});
            skArc(sketch, "E16.24.28.0", {"start": v(-33.63, -71.58) * mm, "mid": v(-33.12, -71.6) * mm, "end": v(-32.72, -71.3) * mm});
            skLineSegment(sketch, "E16.28.28.0", {"start": v(-33.63, -71.58) * mm, "end": v(-33.7, -71.55) * mm});
            skLineSegment(sketch, "E16.31.28.0", {"start": v(-34.46, -73.4) * mm, "end": v(-33.7, -71.55) * mm});
            skLineSegment(sketch, "E16.1.29.0", {"start": v(-19.92, -78.6) * mm, "end": v(-27.1, -76.42) * mm});
            skLineSegment(sketch, "E16.3.29.0", {"start": v(-19.92, -78.6) * mm, "end": v(-19.34, -76.69) * mm});
            skLineSegment(sketch, "E16.6.29.0", {"start": v(-19.34, -76.69) * mm, "end": v(-19.42, -76.66) * mm});
            skArc(sketch, "E16.9.29.0", {"start": v(-19.95, -75.88) * mm, "mid": v(-19.82, -76.37) * mm, "end": v(-19.42, -76.66) * mm});
            skArc(sketch, "E16.13.29.0", {"start": v(-19.95, -75.88) * mm, "mid": v(-20.15, -74.47) * mm, "end": v(-20.99, -73.31) * mm});
            skLineSegment(sketch, "E16.17.29.0", {"start": v(-20.99, -73.31) * mm, "end": v(-23.28, -72.62) * mm});
            skArc(sketch, "E16.20.29.0", {"start": v(-23.28, -72.62) * mm, "mid": v(-24.62, -73.12) * mm, "end": v(-25.57, -74.17) * mm});
            skArc(sketch, "E16.24.29.0", {"start": v(-26.45, -74.53) * mm, "mid": v(-25.95, -74.5) * mm, "end": v(-25.57, -74.17) * mm});
            skLineSegment(sketch, "E16.28.29.0", {"start": v(-26.45, -74.53) * mm, "end": v(-26.52, -74.5) * mm});
            skLineSegment(sketch, "E16.31.29.0", {"start": v(-27.1, -76.42) * mm, "end": v(-26.52, -74.5) * mm});
            skLineSegment(sketch, "E16.1.30.0", {"start": v(-12.12, -80.18) * mm, "end": v(-19.48, -78.71) * mm});
            skLineSegment(sketch, "E16.3.30.0", {"start": v(-12.12, -80.18) * mm, "end": v(-11.73, -78.21) * mm});
            skLineSegment(sketch, "E16.6.30.0", {"start": v(-11.73, -78.21) * mm, "end": v(-11.8, -78.2) * mm});
            skArc(sketch, "E16.9.30.0", {"start": v(-12.41, -77.47) * mm, "mid": v(-12.24, -77.94) * mm, "end": v(-11.8, -78.2) * mm});
            skArc(sketch, "E16.13.30.0", {"start": v(-12.41, -77.47) * mm, "mid": v(-12.76, -76.09) * mm, "end": v(-13.7, -75.02) * mm});
            skLineSegment(sketch, "E16.17.30.0", {"start": v(-13.7, -75.02) * mm, "end": v(-16.05, -74.55) * mm});
            skArc(sketch, "E16.20.30.0", {"start": v(-16.05, -74.55) * mm, "mid": v(-17.33, -75.18) * mm, "end": v(-18.18, -76.32) * mm});
            skArc(sketch, "E16.24.30.0", {"start": v(-19.02, -76.77) * mm, "mid": v(-18.52, -76.7) * mm, "end": v(-18.18, -76.32) * mm});
            skLineSegment(sketch, "E16.28.30.0", {"start": v(-19.02, -76.77) * mm, "end": v(-19.1, -76.75) * mm});
            skLineSegment(sketch, "E16.31.30.0", {"start": v(-19.48, -78.71) * mm, "end": v(-19.1, -76.75) * mm});
            skLineSegment(sketch, "E16.1.31.0", {"start": v(-4.2, -80.98) * mm, "end": v(-11.67, -80.24) * mm});
            skLineSegment(sketch, "E16.3.31.0", {"start": v(-4.2, -80.98) * mm, "end": v(-4.01, -78.99) * mm});
            skLineSegment(sketch, "E16.6.31.0", {"start": v(-4.01, -78.99) * mm, "end": v(-4.09, -78.98) * mm});
            skArc(sketch, "E16.9.31.0", {"start": v(-4.76, -78.31) * mm, "mid": v(-4.54, -78.76) * mm, "end": v(-4.09, -78.98) * mm});
            skArc(sketch, "E16.13.31.0", {"start": v(-4.76, -78.31) * mm, "mid": v(-5.24, -76.97) * mm, "end": v(-6.28, -76) * mm});
            skLineSegment(sketch, "E16.17.31.0", {"start": v(-6.28, -76) * mm, "end": v(-8.67, -75.77) * mm});
            skArc(sketch, "E16.20.31.0", {"start": v(-8.67, -75.77) * mm, "mid": v(-9.88, -76.51) * mm, "end": v(-10.6, -77.73) * mm});
            skArc(sketch, "E16.24.31.0", {"start": v(-11.4, -78.26) * mm, "mid": v(-10.91, -78.14) * mm, "end": v(-10.6, -77.73) * mm});
            skLineSegment(sketch, "E16.28.31.0", {"start": v(-11.4, -78.26) * mm, "end": v(-11.48, -78.25) * mm});
            skLineSegment(sketch, "E16.31.31.0", {"start": v(-11.67, -80.24) * mm, "end": v(-11.48, -78.25) * mm});
            skLineSegment(sketch, "E16.1.32.0", {"start": v(3.75, -81) * mm, "end": v(-3.75, -81) * mm});
            skLineSegment(sketch, "E16.3.32.0", {"start": v(3.75, -81) * mm, "end": v(3.75, -79) * mm});
            skLineSegment(sketch, "E16.6.32.0", {"start": v(3.75, -79) * mm, "end": v(3.67, -79) * mm});
            skArc(sketch, "E16.9.32.0", {"start": v(2.94, -78.4) * mm, "mid": v(3.2, -78.83) * mm, "end": v(3.67, -79) * mm});
            skArc(sketch, "E16.13.32.0", {"start": v(2.94, -78.4) * mm, "mid": v(2.33, -77.11) * mm, "end": v(1.2, -76.25) * mm});
            skLineSegment(sketch, "E16.17.32.0", {"start": v(1.2, -76.25) * mm, "end": v(-1.2, -76.25) * mm});
            skArc(sketch, "E16.20.32.0", {"start": v(-1.2, -76.25) * mm, "mid": v(-2.33, -77.11) * mm, "end": v(-2.94, -78.4) * mm});
            skArc(sketch, "E16.24.32.0", {"start": v(-3.67, -79) * mm, "mid": v(-3.2, -78.83) * mm, "end": v(-2.94, -78.4) * mm});
            skLineSegment(sketch, "E16.28.32.0", {"start": v(-3.67, -79) * mm, "end": v(-3.75, -79) * mm});
            skLineSegment(sketch, "E16.31.32.0", {"start": v(-3.75, -81) * mm, "end": v(-3.75, -79) * mm});
            skLineSegment(sketch, "E16.1.33.0", {"start": v(11.67, -80.24) * mm, "end": v(4.2, -80.98) * mm});
            skLineSegment(sketch, "E16.3.33.0", {"start": v(11.67, -80.24) * mm, "end": v(11.48, -78.25) * mm});
            skLineSegment(sketch, "E16.6.33.0", {"start": v(11.48, -78.25) * mm, "end": v(11.4, -78.26) * mm});
            skArc(sketch, "E16.9.33.0", {"start": v(10.6, -77.73) * mm, "mid": v(10.91, -78.14) * mm, "end": v(11.4, -78.26) * mm});
            skArc(sketch, "E16.13.33.0", {"start": v(10.6, -77.73) * mm, "mid": v(9.88, -76.51) * mm, "end": v(8.67, -75.77) * mm});
            skLineSegment(sketch, "E16.17.33.0", {"start": v(8.67, -75.77) * mm, "end": v(6.28, -76) * mm});
            skArc(sketch, "E16.20.33.0", {"start": v(6.28, -76) * mm, "mid": v(5.24, -76.97) * mm, "end": v(4.76, -78.31) * mm});
            skArc(sketch, "E16.24.33.0", {"start": v(4.09, -78.98) * mm, "mid": v(4.54, -78.76) * mm, "end": v(4.76, -78.31) * mm});
            skLineSegment(sketch, "E16.28.33.0", {"start": v(4.09, -78.98) * mm, "end": v(4.01, -78.99) * mm});
            skLineSegment(sketch, "E16.31.33.0", {"start": v(4.2, -80.98) * mm, "end": v(4.01, -78.99) * mm});
            skLineSegment(sketch, "E16.1.34.0", {"start": v(19.48, -78.71) * mm, "end": v(12.12, -80.18) * mm});
            skLineSegment(sketch, "E16.3.34.0", {"start": v(19.48, -78.71) * mm, "end": v(19.1, -76.75) * mm});
            skLineSegment(sketch, "E16.6.34.0", {"start": v(19.1, -76.75) * mm, "end": v(19.02, -76.77) * mm});
            skArc(sketch, "E16.9.34.0", {"start": v(18.18, -76.32) * mm, "mid": v(18.52, -76.7) * mm, "end": v(19.02, -76.77) * mm});
            skArc(sketch, "E16.13.34.0", {"start": v(18.18, -76.32) * mm, "mid": v(17.33, -75.18) * mm, "end": v(16.05, -74.55) * mm});
            skLineSegment(sketch, "E16.17.34.0", {"start": v(16.05, -74.55) * mm, "end": v(13.7, -75.02) * mm});
            skArc(sketch, "E16.20.34.0", {"start": v(13.7, -75.02) * mm, "mid": v(12.76, -76.09) * mm, "end": v(12.41, -77.47) * mm});
            skArc(sketch, "E16.24.34.0", {"start": v(11.8, -78.2) * mm, "mid": v(12.24, -77.94) * mm, "end": v(12.41, -77.47) * mm});
            skLineSegment(sketch, "E16.28.34.0", {"start": v(11.8, -78.2) * mm, "end": v(11.73, -78.21) * mm});
            skLineSegment(sketch, "E16.31.34.0", {"start": v(12.12, -80.18) * mm, "end": v(11.73, -78.21) * mm});
            skLineSegment(sketch, "E16.1.35.0", {"start": v(27.1, -76.42) * mm, "end": v(19.92, -78.6) * mm});
            skLineSegment(sketch, "E16.3.35.0", {"start": v(27.1, -76.42) * mm, "end": v(26.52, -74.5) * mm});
            skLineSegment(sketch, "E16.6.35.0", {"start": v(26.52, -74.5) * mm, "end": v(26.45, -74.53) * mm});
            skArc(sketch, "E16.9.35.0", {"start": v(25.57, -74.17) * mm, "mid": v(25.95, -74.5) * mm, "end": v(26.45, -74.53) * mm});
            skArc(sketch, "E16.13.35.0", {"start": v(25.57, -74.17) * mm, "mid": v(24.62, -73.12) * mm, "end": v(23.28, -72.62) * mm});
            skLineSegment(sketch, "E16.17.35.0", {"start": v(23.28, -72.62) * mm, "end": v(20.99, -73.31) * mm});
            skArc(sketch, "E16.20.35.0", {"start": v(20.99, -73.31) * mm, "mid": v(20.15, -74.47) * mm, "end": v(19.95, -75.88) * mm});
            skArc(sketch, "E16.24.35.0", {"start": v(19.42, -76.66) * mm, "mid": v(19.82, -76.37) * mm, "end": v(19.95, -75.88) * mm});
            skLineSegment(sketch, "E16.28.35.0", {"start": v(19.42, -76.66) * mm, "end": v(19.34, -76.69) * mm});
            skLineSegment(sketch, "E16.31.35.0", {"start": v(19.92, -78.6) * mm, "end": v(19.34, -76.69) * mm});
            skLineSegment(sketch, "E16.1.36.0", {"start": v(34.46, -73.4) * mm, "end": v(27.53, -76.27) * mm});
            skLineSegment(sketch, "E16.3.36.0", {"start": v(34.46, -73.4) * mm, "end": v(33.7, -71.55) * mm});
            skLineSegment(sketch, "E16.6.36.0", {"start": v(33.7, -71.55) * mm, "end": v(33.63, -71.58) * mm});
            skArc(sketch, "E16.9.36.0", {"start": v(32.72, -71.3) * mm, "mid": v(33.12, -71.6) * mm, "end": v(33.63, -71.58) * mm});
            skArc(sketch, "E16.13.36.0", {"start": v(32.72, -71.3) * mm, "mid": v(31.66, -70.35) * mm, "end": v(30.29, -69.99) * mm});
            skLineSegment(sketch, "E16.17.36.0", {"start": v(30.29, -69.99) * mm, "end": v(28.07, -70.9) * mm});
            skArc(sketch, "E16.20.36.0", {"start": v(28.07, -70.9) * mm, "mid": v(27.36, -72.13) * mm, "end": v(27.29, -73.56) * mm});
            skArc(sketch, "E16.24.36.0", {"start": v(26.84, -74.4) * mm, "mid": v(27.21, -74.05) * mm, "end": v(27.29, -73.56) * mm});
            skLineSegment(sketch, "E16.28.36.0", {"start": v(26.84, -74.4) * mm, "end": v(26.77, -74.42) * mm});
            skLineSegment(sketch, "E16.31.36.0", {"start": v(27.53, -76.27) * mm, "end": v(26.77, -74.42) * mm});
            skLineSegment(sketch, "E16.1.37.0", {"start": v(41.5, -69.67) * mm, "end": v(34.88, -73.2) * mm});
            skLineSegment(sketch, "E16.3.37.0", {"start": v(41.5, -69.67) * mm, "end": v(40.55, -67.9) * mm});
            skLineSegment(sketch, "E16.6.37.0", {"start": v(40.55, -67.9) * mm, "end": v(40.48, -67.94) * mm});
            skArc(sketch, "E16.9.37.0", {"start": v(39.55, -67.76) * mm, "mid": v(39.98, -68.01) * mm, "end": v(40.48, -67.94) * mm});
            skArc(sketch, "E16.13.37.0", {"start": v(39.55, -67.76) * mm, "mid": v(38.4, -66.9) * mm, "end": v(37, -66.68) * mm});
            skLineSegment(sketch, "E16.17.37.0", {"start": v(37, -66.68) * mm, "end": v(34.89, -67.81) * mm});
            skArc(sketch, "E16.20.37.0", {"start": v(34.89, -67.81) * mm, "mid": v(34.3, -69.1) * mm, "end": v(34.37, -70.53) * mm});
            skArc(sketch, "E16.24.37.0", {"start": v(34, -71.4) * mm, "mid": v(34.34, -71.03) * mm, "end": v(34.37, -70.53) * mm});
            skLineSegment(sketch, "E16.28.37.0", {"start": v(34, -71.4) * mm, "end": v(33.93, -71.44) * mm});
            skLineSegment(sketch, "E16.31.37.0", {"start": v(34.88, -73.2) * mm, "end": v(33.93, -71.44) * mm});
            skLineSegment(sketch, "E16.1.38.0", {"start": v(48.12, -65.27) * mm, "end": v(41.88, -69.43) * mm});
            skLineSegment(sketch, "E16.3.38.0", {"start": v(48.12, -65.27) * mm, "end": v(47, -63.6) * mm});
            skLineSegment(sketch, "E16.6.38.0", {"start": v(47, -63.6) * mm, "end": v(46.95, -63.64) * mm});
            skArc(sketch, "E16.9.38.0", {"start": v(46, -63.55) * mm, "mid": v(46.46, -63.77) * mm, "end": v(46.95, -63.64) * mm});
            skArc(sketch, "E16.13.38.0", {"start": v(46, -63.55) * mm, "mid": v(44.78, -62.82) * mm, "end": v(43.36, -62.73) * mm});
            skLineSegment(sketch, "E16.17.38.0", {"start": v(43.36, -62.73) * mm, "end": v(41.37, -64.07) * mm});
            skArc(sketch, "E16.20.38.0", {"start": v(41.37, -64.07) * mm, "mid": v(40.9, -65.41) * mm, "end": v(41.11, -66.82) * mm});
            skArc(sketch, "E16.24.38.0", {"start": v(40.84, -67.73) * mm, "mid": v(41.14, -67.32) * mm, "end": v(41.11, -66.82) * mm});
            skLineSegment(sketch, "E16.28.38.0", {"start": v(40.84, -67.73) * mm, "end": v(40.77, -67.77) * mm});
            skLineSegment(sketch, "E16.31.38.0", {"start": v(41.88, -69.43) * mm, "end": v(40.77, -67.77) * mm});
            skLineSegment(sketch, "E16.1.39.0", {"start": v(54.28, -60.23) * mm, "end": v(48.49, -65) * mm});
            skLineSegment(sketch, "E16.3.39.0", {"start": v(54.28, -60.23) * mm, "end": v(53.02, -58.69) * mm});
            skLineSegment(sketch, "E16.6.39.0", {"start": v(53.02, -58.69) * mm, "end": v(52.96, -58.74) * mm});
            skArc(sketch, "E16.9.39.0", {"start": v(52, -58.74) * mm, "mid": v(52.48, -58.9) * mm, "end": v(52.96, -58.74) * mm});
            skArc(sketch, "E16.13.39.0", {"start": v(52, -58.74) * mm, "mid": v(50.72, -58.13) * mm, "end": v(49.3, -58.18) * mm});
            skLineSegment(sketch, "E16.17.39.0", {"start": v(49.3, -58.18) * mm, "end": v(47.45, -59.7) * mm});
            skArc(sketch, "E16.20.39.0", {"start": v(47.45, -59.7) * mm, "mid": v(47.12, -61.09) * mm, "end": v(47.46, -62.47) * mm});
            skArc(sketch, "E16.24.39.0", {"start": v(47.28, -63.4) * mm, "mid": v(47.54, -62.97) * mm, "end": v(47.46, -62.47) * mm});
            skLineSegment(sketch, "E16.28.39.0", {"start": v(47.28, -63.4) * mm, "end": v(47.22, -63.45) * mm});
            skLineSegment(sketch, "E16.31.39.0", {"start": v(48.49, -65) * mm, "end": v(47.22, -63.45) * mm});
            skLineSegment(sketch, "E16.1.40.0", {"start": v(59.93, -54.62) * mm, "end": v(54.62, -59.93) * mm});
            skLineSegment(sketch, "E16.3.40.0", {"start": v(59.93, -54.62) * mm, "end": v(58.51, -53.2) * mm});
            skLineSegment(sketch, "E16.6.40.0", {"start": v(58.51, -53.2) * mm, "end": v(58.46, -53.26) * mm});
            skArc(sketch, "E16.9.40.0", {"start": v(57.52, -53.36) * mm, "mid": v(58, -53.48) * mm, "end": v(58.46, -53.26) * mm});
            skArc(sketch, "E16.13.40.0", {"start": v(57.52, -53.36) * mm, "mid": v(56.18, -52.88) * mm, "end": v(54.76, -53.07) * mm});
            skLineSegment(sketch, "E16.17.40.0", {"start": v(54.76, -53.07) * mm, "end": v(53.07, -54.76) * mm});
            skArc(sketch, "E16.20.40.0", {"start": v(53.07, -54.76) * mm, "mid": v(52.88, -56.18) * mm, "end": v(53.36, -57.52) * mm});
            skArc(sketch, "E16.24.40.0", {"start": v(53.26, -58.46) * mm, "mid": v(53.48, -58) * mm, "end": v(53.36, -57.52) * mm});
            skLineSegment(sketch, "E16.28.40.0", {"start": v(53.26, -58.46) * mm, "end": v(53.2, -58.51) * mm});
            skLineSegment(sketch, "E16.31.40.0", {"start": v(54.62, -59.93) * mm, "end": v(53.2, -58.51) * mm});
            skLineSegment(sketch, "E16.1.41.0", {"start": v(65, -48.49) * mm, "end": v(60.23, -54.28) * mm});
            skLineSegment(sketch, "E16.3.41.0", {"start": v(65, -48.49) * mm, "end": v(63.45, -47.22) * mm});
            skLineSegment(sketch, "E16.6.41.0", {"start": v(63.45, -47.22) * mm, "end": v(63.4, -47.28) * mm});
            skArc(sketch, "E16.9.41.0", {"start": v(62.47, -47.46) * mm, "mid": v(62.97, -47.54) * mm, "end": v(63.4, -47.28) * mm});
            skArc(sketch, "E16.13.41.0", {"start": v(62.47, -47.46) * mm, "mid": v(61.09, -47.12) * mm, "end": v(59.7, -47.45) * mm});
            skLineSegment(sketch, "E16.17.41.0", {"start": v(59.7, -47.45) * mm, "end": v(58.18, -49.3) * mm});
            skArc(sketch, "E16.20.41.0", {"start": v(58.18, -49.3) * mm, "mid": v(58.13, -50.72) * mm, "end": v(58.74, -52) * mm});
            skArc(sketch, "E16.24.41.0", {"start": v(58.74, -52.96) * mm, "mid": v(58.9, -52.48) * mm, "end": v(58.74, -52) * mm});
            skLineSegment(sketch, "E16.28.41.0", {"start": v(58.74, -52.96) * mm, "end": v(58.69, -53.02) * mm});
            skLineSegment(sketch, "E16.31.41.0", {"start": v(60.23, -54.28) * mm, "end": v(58.69, -53.02) * mm});
            skLineSegment(sketch, "E16.1.42.0", {"start": v(69.43, -41.88) * mm, "end": v(65.27, -48.12) * mm});
            skLineSegment(sketch, "E16.3.42.0", {"start": v(69.43, -41.88) * mm, "end": v(67.77, -40.77) * mm});
            skLineSegment(sketch, "E16.6.42.0", {"start": v(67.77, -40.77) * mm, "end": v(67.73, -40.84) * mm});
            skArc(sketch, "E16.9.42.0", {"start": v(66.82, -41.11) * mm, "mid": v(67.32, -41.14) * mm, "end": v(67.73, -40.84) * mm});
            skArc(sketch, "E16.13.42.0", {"start": v(66.82, -41.11) * mm, "mid": v(65.41, -40.9) * mm, "end": v(64.07, -41.37) * mm});
            skLineSegment(sketch, "E16.17.42.0", {"start": v(64.07, -41.37) * mm, "end": v(62.73, -43.36) * mm});
            skArc(sketch, "E16.20.42.0", {"start": v(62.73, -43.36) * mm, "mid": v(62.82, -44.78) * mm, "end": v(63.55, -46) * mm});
            skArc(sketch, "E16.24.42.0", {"start": v(63.64, -46.95) * mm, "mid": v(63.77, -46.46) * mm, "end": v(63.55, -46) * mm});
            skLineSegment(sketch, "E16.28.42.0", {"start": v(63.64, -46.95) * mm, "end": v(63.6, -47) * mm});
            skLineSegment(sketch, "E16.31.42.0", {"start": v(65.27, -48.12) * mm, "end": v(63.6, -47) * mm});
            skLineSegment(sketch, "E16.1.43.0", {"start": v(73.2, -34.88) * mm, "end": v(69.67, -41.5) * mm});
            skLineSegment(sketch, "E16.3.43.0", {"start": v(73.2, -34.88) * mm, "end": v(71.44, -33.93) * mm});
            skLineSegment(sketch, "E16.6.43.0", {"start": v(71.44, -33.93) * mm, "end": v(71.4, -34) * mm});
            skArc(sketch, "E16.9.43.0", {"start": v(70.53, -34.37) * mm, "mid": v(71.03, -34.34) * mm, "end": v(71.4, -34) * mm});
            skArc(sketch, "E16.13.43.0", {"start": v(70.53, -34.37) * mm, "mid": v(69.1, -34.3) * mm, "end": v(67.81, -34.89) * mm});
            skLineSegment(sketch, "E16.17.43.0", {"start": v(67.81, -34.89) * mm, "end": v(66.68, -37) * mm});
            skArc(sketch, "E16.20.43.0", {"start": v(66.68, -37) * mm, "mid": v(66.9, -38.4) * mm, "end": v(67.76, -39.55) * mm});
            skArc(sketch, "E16.24.43.0", {"start": v(67.94, -40.48) * mm, "mid": v(68.01, -39.98) * mm, "end": v(67.76, -39.55) * mm});
            skLineSegment(sketch, "E16.28.43.0", {"start": v(67.94, -40.48) * mm, "end": v(67.9, -40.55) * mm});
            skLineSegment(sketch, "E16.31.43.0", {"start": v(69.67, -41.5) * mm, "end": v(67.9, -40.55) * mm});
            skLineSegment(sketch, "E16.1.44.0", {"start": v(76.27, -27.53) * mm, "end": v(73.4, -34.46) * mm});
            skLineSegment(sketch, "E16.3.44.0", {"start": v(76.27, -27.53) * mm, "end": v(74.42, -26.77) * mm});
            skLineSegment(sketch, "E16.6.44.0", {"start": v(74.42, -26.77) * mm, "end": v(74.4, -26.84) * mm});
            skArc(sketch, "E16.9.44.0", {"start": v(73.56, -27.29) * mm, "mid": v(74.05, -27.21) * mm, "end": v(74.4, -26.84) * mm});
            skArc(sketch, "E16.13.44.0", {"start": v(73.56, -27.29) * mm, "mid": v(72.13, -27.36) * mm, "end": v(70.9, -28.07) * mm});
            skLineSegment(sketch, "E16.17.44.0", {"start": v(70.9, -28.07) * mm, "end": v(69.99, -30.29) * mm});
            skArc(sketch, "E16.20.44.0", {"start": v(69.99, -30.29) * mm, "mid": v(70.35, -31.66) * mm, "end": v(71.3, -32.72) * mm});
            skArc(sketch, "E16.24.44.0", {"start": v(71.58, -33.63) * mm, "mid": v(71.6, -33.12) * mm, "end": v(71.3, -32.72) * mm});
            skLineSegment(sketch, "E16.28.44.0", {"start": v(71.58, -33.63) * mm, "end": v(71.55, -33.7) * mm});
            skLineSegment(sketch, "E16.31.44.0", {"start": v(73.4, -34.46) * mm, "end": v(71.55, -33.7) * mm});
            skLineSegment(sketch, "E16.1.45.0", {"start": v(78.6, -19.92) * mm, "end": v(76.42, -27.1) * mm});
            skLineSegment(sketch, "E16.3.45.0", {"start": v(78.6, -19.92) * mm, "end": v(76.69, -19.34) * mm});
            skLineSegment(sketch, "E16.6.45.0", {"start": v(76.69, -19.34) * mm, "end": v(76.66, -19.42) * mm});
            skArc(sketch, "E16.9.45.0", {"start": v(75.88, -19.95) * mm, "mid": v(76.37, -19.82) * mm, "end": v(76.66, -19.42) * mm});
            skArc(sketch, "E16.13.45.0", {"start": v(75.88, -19.95) * mm, "mid": v(74.47, -20.15) * mm, "end": v(73.31, -20.99) * mm});
            skLineSegment(sketch, "E16.17.45.0", {"start": v(73.31, -20.99) * mm, "end": v(72.62, -23.28) * mm});
            skArc(sketch, "E16.20.45.0", {"start": v(72.62, -23.28) * mm, "mid": v(73.12, -24.62) * mm, "end": v(74.17, -25.57) * mm});
            skArc(sketch, "E16.24.45.0", {"start": v(74.53, -26.45) * mm, "mid": v(74.5, -25.95) * mm, "end": v(74.17, -25.57) * mm});
            skLineSegment(sketch, "E16.28.45.0", {"start": v(74.53, -26.45) * mm, "end": v(74.5, -26.52) * mm});
            skLineSegment(sketch, "E16.31.45.0", {"start": v(76.42, -27.1) * mm, "end": v(74.5, -26.52) * mm});
            skLineSegment(sketch, "E16.1.46.0", {"start": v(80.18, -12.12) * mm, "end": v(78.71, -19.48) * mm});
            skLineSegment(sketch, "E16.3.46.0", {"start": v(80.18, -12.12) * mm, "end": v(78.21, -11.73) * mm});
            skLineSegment(sketch, "E16.6.46.0", {"start": v(78.21, -11.73) * mm, "end": v(78.2, -11.8) * mm});
            skArc(sketch, "E16.9.46.0", {"start": v(77.47, -12.41) * mm, "mid": v(77.94, -12.24) * mm, "end": v(78.2, -11.8) * mm});
            skArc(sketch, "E16.13.46.0", {"start": v(77.47, -12.41) * mm, "mid": v(76.09, -12.76) * mm, "end": v(75.02, -13.7) * mm});
            skLineSegment(sketch, "E16.17.46.0", {"start": v(75.02, -13.7) * mm, "end": v(74.55, -16.05) * mm});
            skArc(sketch, "E16.20.46.0", {"start": v(74.55, -16.05) * mm, "mid": v(75.18, -17.33) * mm, "end": v(76.32, -18.18) * mm});
            skArc(sketch, "E16.24.46.0", {"start": v(76.77, -19.02) * mm, "mid": v(76.7, -18.52) * mm, "end": v(76.32, -18.18) * mm});
            skLineSegment(sketch, "E16.28.46.0", {"start": v(76.77, -19.02) * mm, "end": v(76.75, -19.1) * mm});
            skLineSegment(sketch, "E16.31.46.0", {"start": v(78.71, -19.48) * mm, "end": v(76.75, -19.1) * mm});
            skLineSegment(sketch, "E16.1.47.0", {"start": v(80.98, -4.2) * mm, "end": v(80.24, -11.67) * mm});
            skLineSegment(sketch, "E16.3.47.0", {"start": v(80.98, -4.2) * mm, "end": v(78.99, -4.01) * mm});
            skLineSegment(sketch, "E16.6.47.0", {"start": v(78.99, -4.01) * mm, "end": v(78.98, -4.09) * mm});
            skArc(sketch, "E16.9.47.0", {"start": v(78.31, -4.76) * mm, "mid": v(78.76, -4.54) * mm, "end": v(78.98, -4.09) * mm});
            skArc(sketch, "E16.13.47.0", {"start": v(78.31, -4.76) * mm, "mid": v(76.97, -5.24) * mm, "end": v(76, -6.28) * mm});
            skLineSegment(sketch, "E16.17.47.0", {"start": v(76, -6.28) * mm, "end": v(75.77, -8.67) * mm});
            skArc(sketch, "E16.20.47.0", {"start": v(75.77, -8.67) * mm, "mid": v(76.51, -9.88) * mm, "end": v(77.73, -10.6) * mm});
            skArc(sketch, "E16.24.47.0", {"start": v(78.26, -11.4) * mm, "mid": v(78.14, -10.91) * mm, "end": v(77.73, -10.6) * mm});
            skLineSegment(sketch, "E16.28.47.0", {"start": v(78.26, -11.4) * mm, "end": v(78.25, -11.48) * mm});
            skLineSegment(sketch, "E16.31.47.0", {"start": v(80.24, -11.67) * mm, "end": v(78.25, -11.48) * mm});
            skLineSegment(sketch, "E16.1.48.0", {"start": v(81, 3.75) * mm, "end": v(81, -3.75) * mm});
            skLineSegment(sketch, "E16.3.48.0", {"start": v(81, 3.75) * mm, "end": v(79, 3.75) * mm});
            skLineSegment(sketch, "E16.6.48.0", {"start": v(79, 3.75) * mm, "end": v(79, 3.67) * mm});
            skArc(sketch, "E16.9.48.0", {"start": v(78.4, 2.94) * mm, "mid": v(78.83, 3.2) * mm, "end": v(79, 3.67) * mm});
            skArc(sketch, "E16.13.48.0", {"start": v(78.4, 2.94) * mm, "mid": v(77.11, 2.33) * mm, "end": v(76.25, 1.2) * mm});
            skLineSegment(sketch, "E16.17.48.0", {"start": v(76.25, 1.2) * mm, "end": v(76.25, -1.2) * mm});
            skArc(sketch, "E16.20.48.0", {"start": v(76.25, -1.2) * mm, "mid": v(77.11, -2.33) * mm, "end": v(78.4, -2.94) * mm});
            skArc(sketch, "E16.24.48.0", {"start": v(79, -3.67) * mm, "mid": v(78.83, -3.2) * mm, "end": v(78.4, -2.94) * mm});
            skLineSegment(sketch, "E16.28.48.0", {"start": v(79, -3.67) * mm, "end": v(79, -3.75) * mm});
            skLineSegment(sketch, "E16.31.48.0", {"start": v(81, -3.75) * mm, "end": v(79, -3.75) * mm});
            skLineSegment(sketch, "E16.1.49.0", {"start": v(80.24, 11.67) * mm, "end": v(80.98, 4.2) * mm});
            skLineSegment(sketch, "E16.3.49.0", {"start": v(80.24, 11.67) * mm, "end": v(78.25, 11.48) * mm});
            skLineSegment(sketch, "E16.6.49.0", {"start": v(78.25, 11.48) * mm, "end": v(78.26, 11.4) * mm});
            skArc(sketch, "E16.9.49.0", {"start": v(77.73, 10.6) * mm, "mid": v(78.14, 10.91) * mm, "end": v(78.26, 11.4) * mm});
            skArc(sketch, "E16.13.49.0", {"start": v(77.73, 10.6) * mm, "mid": v(76.51, 9.88) * mm, "end": v(75.77, 8.67) * mm});
            skLineSegment(sketch, "E16.17.49.0", {"start": v(75.77, 8.67) * mm, "end": v(76, 6.28) * mm});
            skArc(sketch, "E16.20.49.0", {"start": v(76, 6.28) * mm, "mid": v(76.97, 5.24) * mm, "end": v(78.31, 4.76) * mm});
            skArc(sketch, "E16.24.49.0", {"start": v(78.98, 4.09) * mm, "mid": v(78.76, 4.54) * mm, "end": v(78.31, 4.76) * mm});
            skLineSegment(sketch, "E16.28.49.0", {"start": v(78.98, 4.09) * mm, "end": v(78.99, 4.01) * mm});
            skLineSegment(sketch, "E16.31.49.0", {"start": v(80.98, 4.2) * mm, "end": v(78.99, 4.01) * mm});
            skLineSegment(sketch, "E16.1.50.0", {"start": v(78.71, 19.48) * mm, "end": v(80.18, 12.12) * mm});
            skLineSegment(sketch, "E16.3.50.0", {"start": v(78.71, 19.48) * mm, "end": v(76.75, 19.1) * mm});
            skLineSegment(sketch, "E16.6.50.0", {"start": v(76.75, 19.1) * mm, "end": v(76.77, 19.02) * mm});
            skArc(sketch, "E16.9.50.0", {"start": v(76.32, 18.18) * mm, "mid": v(76.7, 18.52) * mm, "end": v(76.77, 19.02) * mm});
            skArc(sketch, "E16.13.50.0", {"start": v(76.32, 18.18) * mm, "mid": v(75.18, 17.33) * mm, "end": v(74.55, 16.05) * mm});
            skLineSegment(sketch, "E16.17.50.0", {"start": v(74.55, 16.05) * mm, "end": v(75.02, 13.7) * mm});
            skArc(sketch, "E16.20.50.0", {"start": v(75.02, 13.7) * mm, "mid": v(76.09, 12.76) * mm, "end": v(77.47, 12.41) * mm});
            skArc(sketch, "E16.24.50.0", {"start": v(78.2, 11.8) * mm, "mid": v(77.94, 12.24) * mm, "end": v(77.47, 12.41) * mm});
            skLineSegment(sketch, "E16.28.50.0", {"start": v(78.2, 11.8) * mm, "end": v(78.21, 11.73) * mm});
            skLineSegment(sketch, "E16.31.50.0", {"start": v(80.18, 12.12) * mm, "end": v(78.21, 11.73) * mm});
            skLineSegment(sketch, "E16.1.51.0", {"start": v(76.42, 27.1) * mm, "end": v(78.6, 19.92) * mm});
            skLineSegment(sketch, "E16.3.51.0", {"start": v(76.42, 27.1) * mm, "end": v(74.5, 26.52) * mm});
            skLineSegment(sketch, "E16.6.51.0", {"start": v(74.5, 26.52) * mm, "end": v(74.53, 26.45) * mm});
            skArc(sketch, "E16.9.51.0", {"start": v(74.17, 25.57) * mm, "mid": v(74.5, 25.95) * mm, "end": v(74.53, 26.45) * mm});
            skArc(sketch, "E16.13.51.0", {"start": v(74.17, 25.57) * mm, "mid": v(73.12, 24.62) * mm, "end": v(72.62, 23.28) * mm});
            skLineSegment(sketch, "E16.17.51.0", {"start": v(72.62, 23.28) * mm, "end": v(73.31, 20.99) * mm});
            skArc(sketch, "E16.20.51.0", {"start": v(73.31, 20.99) * mm, "mid": v(74.47, 20.15) * mm, "end": v(75.88, 19.95) * mm});
            skArc(sketch, "E16.24.51.0", {"start": v(76.66, 19.42) * mm, "mid": v(76.37, 19.82) * mm, "end": v(75.88, 19.95) * mm});
            skLineSegment(sketch, "E16.28.51.0", {"start": v(76.66, 19.42) * mm, "end": v(76.69, 19.34) * mm});
            skLineSegment(sketch, "E16.31.51.0", {"start": v(78.6, 19.92) * mm, "end": v(76.69, 19.34) * mm});
            skLineSegment(sketch, "E16.1.52.0", {"start": v(73.4, 34.46) * mm, "end": v(76.27, 27.53) * mm});
            skLineSegment(sketch, "E16.3.52.0", {"start": v(73.4, 34.46) * mm, "end": v(71.55, 33.7) * mm});
            skLineSegment(sketch, "E16.6.52.0", {"start": v(71.55, 33.7) * mm, "end": v(71.58, 33.63) * mm});
            skArc(sketch, "E16.9.52.0", {"start": v(71.3, 32.72) * mm, "mid": v(71.6, 33.12) * mm, "end": v(71.58, 33.63) * mm});
            skArc(sketch, "E16.13.52.0", {"start": v(71.3, 32.72) * mm, "mid": v(70.35, 31.66) * mm, "end": v(69.99, 30.29) * mm});
            skLineSegment(sketch, "E16.17.52.0", {"start": v(69.99, 30.29) * mm, "end": v(70.9, 28.07) * mm});
            skArc(sketch, "E16.20.52.0", {"start": v(70.9, 28.07) * mm, "mid": v(72.13, 27.36) * mm, "end": v(73.56, 27.29) * mm});
            skArc(sketch, "E16.24.52.0", {"start": v(74.4, 26.84) * mm, "mid": v(74.05, 27.21) * mm, "end": v(73.56, 27.29) * mm});
            skLineSegment(sketch, "E16.28.52.0", {"start": v(74.4, 26.84) * mm, "end": v(74.42, 26.77) * mm});
            skLineSegment(sketch, "E16.31.52.0", {"start": v(76.27, 27.53) * mm, "end": v(74.42, 26.77) * mm});
            skLineSegment(sketch, "E16.1.53.0", {"start": v(69.67, 41.5) * mm, "end": v(73.2, 34.88) * mm});
            skLineSegment(sketch, "E16.3.53.0", {"start": v(69.67, 41.5) * mm, "end": v(67.9, 40.55) * mm});
            skLineSegment(sketch, "E16.6.53.0", {"start": v(67.9, 40.55) * mm, "end": v(67.94, 40.48) * mm});
            skArc(sketch, "E16.9.53.0", {"start": v(67.76, 39.55) * mm, "mid": v(68.01, 39.98) * mm, "end": v(67.94, 40.48) * mm});
            skArc(sketch, "E16.13.53.0", {"start": v(67.76, 39.55) * mm, "mid": v(66.9, 38.4) * mm, "end": v(66.68, 37) * mm});
            skLineSegment(sketch, "E16.17.53.0", {"start": v(66.68, 37) * mm, "end": v(67.81, 34.89) * mm});
            skArc(sketch, "E16.20.53.0", {"start": v(67.81, 34.89) * mm, "mid": v(69.1, 34.3) * mm, "end": v(70.53, 34.37) * mm});
            skArc(sketch, "E16.24.53.0", {"start": v(71.4, 34) * mm, "mid": v(71.03, 34.34) * mm, "end": v(70.53, 34.37) * mm});
            skLineSegment(sketch, "E16.28.53.0", {"start": v(71.4, 34) * mm, "end": v(71.44, 33.93) * mm});
            skLineSegment(sketch, "E16.31.53.0", {"start": v(73.2, 34.88) * mm, "end": v(71.44, 33.93) * mm});
            skLineSegment(sketch, "E16.1.54.0", {"start": v(65.27, 48.12) * mm, "end": v(69.43, 41.88) * mm});
            skLineSegment(sketch, "E16.3.54.0", {"start": v(65.27, 48.12) * mm, "end": v(63.6, 47) * mm});
            skLineSegment(sketch, "E16.6.54.0", {"start": v(63.6, 47) * mm, "end": v(63.64, 46.95) * mm});
            skArc(sketch, "E16.9.54.0", {"start": v(63.55, 46) * mm, "mid": v(63.77, 46.46) * mm, "end": v(63.64, 46.95) * mm});
            skArc(sketch, "E16.13.54.0", {"start": v(63.55, 46) * mm, "mid": v(62.82, 44.78) * mm, "end": v(62.73, 43.36) * mm});
            skLineSegment(sketch, "E16.17.54.0", {"start": v(62.73, 43.36) * mm, "end": v(64.07, 41.37) * mm});
            skArc(sketch, "E16.20.54.0", {"start": v(64.07, 41.37) * mm, "mid": v(65.41, 40.9) * mm, "end": v(66.82, 41.11) * mm});
            skArc(sketch, "E16.24.54.0", {"start": v(67.73, 40.84) * mm, "mid": v(67.32, 41.14) * mm, "end": v(66.82, 41.11) * mm});
            skLineSegment(sketch, "E16.28.54.0", {"start": v(67.73, 40.84) * mm, "end": v(67.77, 40.77) * mm});
            skLineSegment(sketch, "E16.31.54.0", {"start": v(69.43, 41.88) * mm, "end": v(67.77, 40.77) * mm});
            skLineSegment(sketch, "E16.1.55.0", {"start": v(60.23, 54.28) * mm, "end": v(65, 48.49) * mm});
            skLineSegment(sketch, "E16.3.55.0", {"start": v(60.23, 54.28) * mm, "end": v(58.69, 53.02) * mm});
            skLineSegment(sketch, "E16.6.55.0", {"start": v(58.69, 53.02) * mm, "end": v(58.74, 52.96) * mm});
            skArc(sketch, "E16.9.55.0", {"start": v(58.74, 52) * mm, "mid": v(58.9, 52.48) * mm, "end": v(58.74, 52.96) * mm});
            skArc(sketch, "E16.13.55.0", {"start": v(58.74, 52) * mm, "mid": v(58.13, 50.72) * mm, "end": v(58.18, 49.3) * mm});
            skLineSegment(sketch, "E16.17.55.0", {"start": v(58.18, 49.3) * mm, "end": v(59.7, 47.45) * mm});
            skArc(sketch, "E16.20.55.0", {"start": v(59.7, 47.45) * mm, "mid": v(61.09, 47.12) * mm, "end": v(62.47, 47.46) * mm});
            skArc(sketch, "E16.24.55.0", {"start": v(63.4, 47.28) * mm, "mid": v(62.97, 47.54) * mm, "end": v(62.47, 47.46) * mm});
            skLineSegment(sketch, "E16.28.55.0", {"start": v(63.4, 47.28) * mm, "end": v(63.45, 47.22) * mm});
            skLineSegment(sketch, "E16.31.55.0", {"start": v(65, 48.49) * mm, "end": v(63.45, 47.22) * mm});
            skLineSegment(sketch, "E16.1.56.0", {"start": v(54.62, 59.93) * mm, "end": v(59.93, 54.62) * mm});
            skLineSegment(sketch, "E16.3.56.0", {"start": v(54.62, 59.93) * mm, "end": v(53.2, 58.51) * mm});
            skLineSegment(sketch, "E16.6.56.0", {"start": v(53.2, 58.51) * mm, "end": v(53.26, 58.46) * mm});
            skArc(sketch, "E16.9.56.0", {"start": v(53.36, 57.52) * mm, "mid": v(53.48, 58) * mm, "end": v(53.26, 58.46) * mm});
            skArc(sketch, "E16.13.56.0", {"start": v(53.36, 57.52) * mm, "mid": v(52.88, 56.18) * mm, "end": v(53.07, 54.76) * mm});
            skLineSegment(sketch, "E16.17.56.0", {"start": v(53.07, 54.76) * mm, "end": v(54.76, 53.07) * mm});
            skArc(sketch, "E16.20.56.0", {"start": v(54.76, 53.07) * mm, "mid": v(56.18, 52.88) * mm, "end": v(57.52, 53.36) * mm});
            skArc(sketch, "E16.24.56.0", {"start": v(58.46, 53.26) * mm, "mid": v(58, 53.48) * mm, "end": v(57.52, 53.36) * mm});
            skLineSegment(sketch, "E16.28.56.0", {"start": v(58.46, 53.26) * mm, "end": v(58.51, 53.2) * mm});
            skLineSegment(sketch, "E16.31.56.0", {"start": v(59.93, 54.62) * mm, "end": v(58.51, 53.2) * mm});
            skLineSegment(sketch, "E16.1.57.0", {"start": v(48.49, 65) * mm, "end": v(54.28, 60.23) * mm});
            skLineSegment(sketch, "E16.3.57.0", {"start": v(48.49, 65) * mm, "end": v(47.22, 63.45) * mm});
            skLineSegment(sketch, "E16.6.57.0", {"start": v(47.22, 63.45) * mm, "end": v(47.28, 63.4) * mm});
            skArc(sketch, "E16.9.57.0", {"start": v(47.46, 62.47) * mm, "mid": v(47.54, 62.97) * mm, "end": v(47.28, 63.4) * mm});
            skArc(sketch, "E16.13.57.0", {"start": v(47.46, 62.47) * mm, "mid": v(47.12, 61.09) * mm, "end": v(47.45, 59.7) * mm});
            skLineSegment(sketch, "E16.17.57.0", {"start": v(47.45, 59.7) * mm, "end": v(49.3, 58.18) * mm});
            skArc(sketch, "E16.20.57.0", {"start": v(49.3, 58.18) * mm, "mid": v(50.72, 58.13) * mm, "end": v(52, 58.74) * mm});
            skArc(sketch, "E16.24.57.0", {"start": v(52.96, 58.74) * mm, "mid": v(52.48, 58.9) * mm, "end": v(52, 58.74) * mm});
            skLineSegment(sketch, "E16.28.57.0", {"start": v(52.96, 58.74) * mm, "end": v(53.02, 58.69) * mm});
            skLineSegment(sketch, "E16.31.57.0", {"start": v(54.28, 60.23) * mm, "end": v(53.02, 58.69) * mm});
            skLineSegment(sketch, "E16.1.58.0", {"start": v(41.88, 69.43) * mm, "end": v(48.12, 65.27) * mm});
            skLineSegment(sketch, "E16.3.58.0", {"start": v(41.88, 69.43) * mm, "end": v(40.77, 67.77) * mm});
            skLineSegment(sketch, "E16.6.58.0", {"start": v(40.77, 67.77) * mm, "end": v(40.84, 67.73) * mm});
            skArc(sketch, "E16.9.58.0", {"start": v(41.11, 66.82) * mm, "mid": v(41.14, 67.32) * mm, "end": v(40.84, 67.73) * mm});
            skArc(sketch, "E16.13.58.0", {"start": v(41.11, 66.82) * mm, "mid": v(40.9, 65.41) * mm, "end": v(41.37, 64.07) * mm});
            skLineSegment(sketch, "E16.17.58.0", {"start": v(41.37, 64.07) * mm, "end": v(43.36, 62.73) * mm});
            skArc(sketch, "E16.20.58.0", {"start": v(43.36, 62.73) * mm, "mid": v(44.78, 62.82) * mm, "end": v(46, 63.55) * mm});
            skArc(sketch, "E16.24.58.0", {"start": v(46.95, 63.64) * mm, "mid": v(46.46, 63.77) * mm, "end": v(46, 63.55) * mm});
            skLineSegment(sketch, "E16.28.58.0", {"start": v(46.95, 63.64) * mm, "end": v(47, 63.6) * mm});
            skLineSegment(sketch, "E16.31.58.0", {"start": v(48.12, 65.27) * mm, "end": v(47, 63.6) * mm});
            skLineSegment(sketch, "E16.1.59.0", {"start": v(34.88, 73.2) * mm, "end": v(41.5, 69.67) * mm});
            skLineSegment(sketch, "E16.3.59.0", {"start": v(34.88, 73.2) * mm, "end": v(33.93, 71.44) * mm});
            skLineSegment(sketch, "E16.6.59.0", {"start": v(33.93, 71.44) * mm, "end": v(34, 71.4) * mm});
            skArc(sketch, "E16.9.59.0", {"start": v(34.37, 70.53) * mm, "mid": v(34.34, 71.03) * mm, "end": v(34, 71.4) * mm});
            skArc(sketch, "E16.13.59.0", {"start": v(34.37, 70.53) * mm, "mid": v(34.3, 69.1) * mm, "end": v(34.89, 67.81) * mm});
            skLineSegment(sketch, "E16.17.59.0", {"start": v(34.89, 67.81) * mm, "end": v(37, 66.68) * mm});
            skArc(sketch, "E16.20.59.0", {"start": v(37, 66.68) * mm, "mid": v(38.4, 66.9) * mm, "end": v(39.55, 67.76) * mm});
            skArc(sketch, "E16.24.59.0", {"start": v(40.48, 67.94) * mm, "mid": v(39.98, 68.01) * mm, "end": v(39.55, 67.76) * mm});
            skLineSegment(sketch, "E16.28.59.0", {"start": v(40.48, 67.94) * mm, "end": v(40.55, 67.9) * mm});
            skLineSegment(sketch, "E16.31.59.0", {"start": v(41.5, 69.67) * mm, "end": v(40.55, 67.9) * mm});
            skLineSegment(sketch, "E16.1.60.0", {"start": v(27.53, 76.27) * mm, "end": v(34.46, 73.4) * mm});
            skLineSegment(sketch, "E16.3.60.0", {"start": v(27.53, 76.27) * mm, "end": v(26.77, 74.42) * mm});
            skLineSegment(sketch, "E16.6.60.0", {"start": v(26.77, 74.42) * mm, "end": v(26.84, 74.4) * mm});
            skArc(sketch, "E16.9.60.0", {"start": v(27.29, 73.56) * mm, "mid": v(27.21, 74.05) * mm, "end": v(26.84, 74.4) * mm});
            skArc(sketch, "E16.13.60.0", {"start": v(27.29, 73.56) * mm, "mid": v(27.36, 72.13) * mm, "end": v(28.07, 70.9) * mm});
            skLineSegment(sketch, "E16.17.60.0", {"start": v(28.07, 70.9) * mm, "end": v(30.29, 69.99) * mm});
            skArc(sketch, "E16.20.60.0", {"start": v(30.29, 69.99) * mm, "mid": v(31.66, 70.35) * mm, "end": v(32.72, 71.3) * mm});
            skArc(sketch, "E16.24.60.0", {"start": v(33.63, 71.58) * mm, "mid": v(33.12, 71.6) * mm, "end": v(32.72, 71.3) * mm});
            skLineSegment(sketch, "E16.28.60.0", {"start": v(33.63, 71.58) * mm, "end": v(33.7, 71.55) * mm});
            skLineSegment(sketch, "E16.31.60.0", {"start": v(34.46, 73.4) * mm, "end": v(33.7, 71.55) * mm});
            skLineSegment(sketch, "E16.1.61.0", {"start": v(19.92, 78.6) * mm, "end": v(27.1, 76.42) * mm});
            skLineSegment(sketch, "E16.3.61.0", {"start": v(19.92, 78.6) * mm, "end": v(19.34, 76.69) * mm});
            skLineSegment(sketch, "E16.6.61.0", {"start": v(19.34, 76.69) * mm, "end": v(19.42, 76.66) * mm});
            skArc(sketch, "E16.9.61.0", {"start": v(19.95, 75.88) * mm, "mid": v(19.82, 76.37) * mm, "end": v(19.42, 76.66) * mm});
            skArc(sketch, "E16.13.61.0", {"start": v(19.95, 75.88) * mm, "mid": v(20.15, 74.47) * mm, "end": v(20.99, 73.31) * mm});
            skLineSegment(sketch, "E16.17.61.0", {"start": v(20.99, 73.31) * mm, "end": v(23.28, 72.62) * mm});
            skArc(sketch, "E16.20.61.0", {"start": v(23.28, 72.62) * mm, "mid": v(24.62, 73.12) * mm, "end": v(25.57, 74.17) * mm});
            skArc(sketch, "E16.24.61.0", {"start": v(26.45, 74.53) * mm, "mid": v(25.95, 74.5) * mm, "end": v(25.57, 74.17) * mm});
            skLineSegment(sketch, "E16.28.61.0", {"start": v(26.45, 74.53) * mm, "end": v(26.52, 74.5) * mm});
            skLineSegment(sketch, "E16.31.61.0", {"start": v(27.1, 76.42) * mm, "end": v(26.52, 74.5) * mm});
            skLineSegment(sketch, "E16.1.62.0", {"start": v(12.12, 80.18) * mm, "end": v(19.48, 78.71) * mm});
            skLineSegment(sketch, "E16.3.62.0", {"start": v(12.12, 80.18) * mm, "end": v(11.73, 78.21) * mm});
            skLineSegment(sketch, "E16.6.62.0", {"start": v(11.73, 78.21) * mm, "end": v(11.8, 78.2) * mm});
            skArc(sketch, "E16.9.62.0", {"start": v(12.41, 77.47) * mm, "mid": v(12.24, 77.94) * mm, "end": v(11.8, 78.2) * mm});
            skArc(sketch, "E16.13.62.0", {"start": v(12.41, 77.47) * mm, "mid": v(12.76, 76.09) * mm, "end": v(13.7, 75.02) * mm});
            skLineSegment(sketch, "E16.17.62.0", {"start": v(13.7, 75.02) * mm, "end": v(16.05, 74.55) * mm});
            skArc(sketch, "E16.20.62.0", {"start": v(16.05, 74.55) * mm, "mid": v(17.33, 75.18) * mm, "end": v(18.18, 76.32) * mm});
            skArc(sketch, "E16.24.62.0", {"start": v(19.02, 76.77) * mm, "mid": v(18.52, 76.7) * mm, "end": v(18.18, 76.32) * mm});
            skLineSegment(sketch, "E16.28.62.0", {"start": v(19.02, 76.77) * mm, "end": v(19.1, 76.75) * mm});
            skLineSegment(sketch, "E16.31.62.0", {"start": v(19.48, 78.71) * mm, "end": v(19.1, 76.75) * mm});
            skLineSegment(sketch, "E16.1.63.0", {"start": v(4.2, 80.98) * mm, "end": v(11.67, 80.24) * mm});
            skLineSegment(sketch, "E16.3.63.0", {"start": v(4.2, 80.98) * mm, "end": v(4.01, 78.99) * mm});
            skLineSegment(sketch, "E16.6.63.0", {"start": v(4.01, 78.99) * mm, "end": v(4.09, 78.98) * mm});
            skArc(sketch, "E16.9.63.0", {"start": v(4.76, 78.31) * mm, "mid": v(4.54, 78.76) * mm, "end": v(4.09, 78.98) * mm});
            skArc(sketch, "E16.13.63.0", {"start": v(4.76, 78.31) * mm, "mid": v(5.24, 76.97) * mm, "end": v(6.28, 76) * mm});
            skLineSegment(sketch, "E16.17.63.0", {"start": v(6.28, 76) * mm, "end": v(8.67, 75.77) * mm});
            skArc(sketch, "E16.20.63.0", {"start": v(8.67, 75.77) * mm, "mid": v(9.88, 76.51) * mm, "end": v(10.6, 77.73) * mm});
            skArc(sketch, "E16.24.63.0", {"start": v(11.4, 78.26) * mm, "mid": v(10.91, 78.14) * mm, "end": v(10.6, 77.73) * mm});
            skLineSegment(sketch, "E16.28.63.0", {"start": v(11.4, 78.26) * mm, "end": v(11.48, 78.25) * mm});
            skLineSegment(sketch, "E16.31.63.0", {"start": v(11.67, 80.24) * mm, "end": v(11.48, 78.25) * mm});
            skSolve(sketch);
        }
        {
            var Q0;
            Q0 = qSketchRegion(id + "F3", true);
            extrude(context, id + "F4", {"entities" : qUnion([Q0]), "operationType" : NewBodyOperationType.REMOVE, "endBound" : BoundingType.THROUGH_ALL, "oppositeDirection" : true, "depth" : 25.4 * mm});
        }
        {
            var Q0;
            Q0=qCreatedBy(makeId("Right.planeOp"),FACE);
            var sketch = newSketch(context, id + "F5", { "sketchPlane" : qUnion([Q0])});
            skLineSegment(sketch, "E17.bottom", {"start": v(0, 80.61) * mm, "end": v(1.5, 80.61) * mm});
            skLineSegment(sketch, "E17.top", {"start": v(0, 75.61) * mm, "end": v(1.5, 75.61) * mm});
            skLineSegment(sketch, "E17.left", {"start": v(0, 80.61) * mm, "end": v(0, 75.61) * mm});
            skLineSegment(sketch, "E17.right", {"start": v(1.5, 80.61) * mm, "end": v(1.5, 75.61) * mm});
            skLineSegment(sketch, "E18", {"start": v(1.5, 80.61) * mm, "end": v(0.86, 83.01) * mm});
            skLineSegment(sketch, "E19", {"start": v(0.86, 83.01) * mm, "end": v(-0.6, 82.62) * mm});
            skLineSegment(sketch, "E20", {"start": v(-0.6, 82.62) * mm, "end": v(0.05, 80.22) * mm});
            skLineSegment(sketch, "E21", {"start": v(0.05, 80.22) * mm, "end": v(1.5, 80.61) * mm});
            skLineSegment(sketch, "E22", {"start": v(15, 102.47) * mm, "end": v(15, -10.74) * mm, "construction": true});
            skLineSegment(sketch, "E23.MirrorCS", {"start": v(29.14, 83.01) * mm, "end": v(30.6, 82.62) * mm});
            skLineSegment(sketch, "E24.MirrorCS", {"start": v(28.5, 80.61) * mm, "end": v(29.14, 83.01) * mm});
            skLineSegment(sketch, "E25.MirrorCS", {"start": v(30.6, 82.62) * mm, "end": v(29.95, 80.22) * mm});
            skLineSegment(sketch, "E26.MirrorCS", {"start": v(28.5, 80.61) * mm, "end": v(28.5, 75.61) * mm});
            skLineSegment(sketch, "E27.MirrorCS", {"start": v(30, 75.61) * mm, "end": v(28.5, 75.61) * mm});
            skLineSegment(sketch, "E28.MirrorCS", {"start": v(30, 80.61) * mm, "end": v(30, 75.61) * mm});
            skLineSegment(sketch, "E29.MirrorCS", {"start": v(29.95, 80.22) * mm, "end": v(28.5, 80.61) * mm});
            skLineSegment(sketch, "E30.MirrorCS", {"start": v(30, 80.61) * mm, "end": v(28.5, 80.61) * mm});
            skSolve(sketch);
        }
        {
            var Q0;
            Q0 = qSketchRegion(id + "F5", true);
            var Q1;
            Q1=sQuery(id+"F2.wireOp",EDGE,"E7");
            revolve(context, id + "F6", {"operationType" : NewBodyOperationType.ADD, "entities" : qUnion([Q0]), "axis" : qUnion([Q1]), "revolveType" : RevolveType.FULL});
        }
    });
